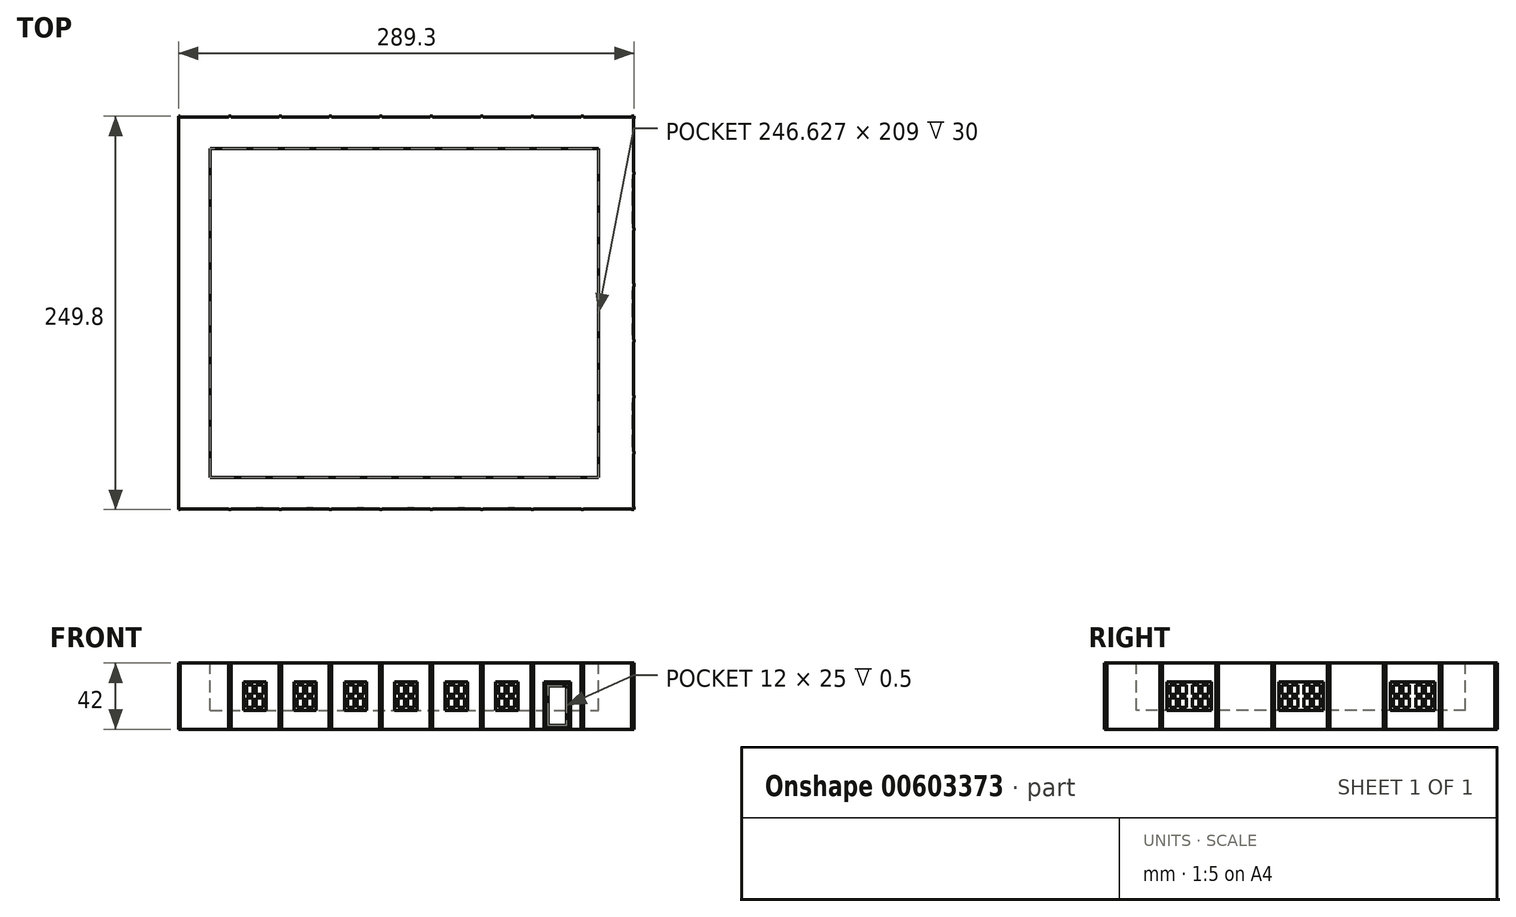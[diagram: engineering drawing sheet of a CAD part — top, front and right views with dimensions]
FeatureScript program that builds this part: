
annotation { "Feature Type Name" : "Feature", "Feature Type Description" : "" }
export const myFeature = defineFeature(function(context is Context, id is Id, definition is map)
    precondition{}
    {
        {
            var Q0;
            Q0=qCreatedBy(makeId("Top.planeOp"),FACE);
            var sketch = newSketch(context, id + "F0", { "sketchPlane" : qUnion([Q0])});
            skLineSegment(sketch, "E0", {"start": v(0, -140.86) * mm, "end": v(288.9, -140.86) * mm});
            skLineSegment(sketch, "E1", {"start": v(288.9, -140.86) * mm, "end": v(288.9, 108.14) * mm});
            skLineSegment(sketch, "E2", {"start": v(288.9, 108.14) * mm, "end": v(0, 108.14) * mm});
            skLineSegment(sketch, "E3", {"start": v(0, 108.14) * mm, "end": v(0, -140.86) * mm});
            skSolve(sketch);
        }
        {
            var Q0;
            Q0=makeQuery(id+"F0.imprint","IMPRINT",FACE,{"disambiguationData":[TD([[makeQuery(id+"F0.imprint","IMPRINT",EDGE,{"derivedFrom":sQuery(id+"F0.wireOp",EDGE,"E0")}),1.0]])]});
            extrude(context, id + "F1", {"entities" : qUnion([Q0]), "depth" : 42 * mm, "offsetDistance" : 25 * mm});
        }
        {
            var Q0;
            Q0=makeQuery(id+"F9.boolean.opBoolean","MERGE",FACE,{"derivedFrom":[makeQuery(id+"F8.boolean.opBoolean","MERGE",FACE,{"derivedFrom":[makeQuery(id+"FKC5EGcOAujftDL_1.boolean.opBoolean","MERGE",FACE,{"derivedFrom":[makeQuery(id+"F7.boolean.opBoolean","MERGE",FACE,{"derivedFrom":[makeQuery(id+"F1.opExtrude","CAP_FACE",FACE,{"disambiguationData":[OSD([sQuery(id+"F0.wireOp",EDGE,"8xd5dAzC-Wqp6-h7tH-H7tE-NGzX7Ft5cmzh"),sQuery(id+"F0.wireOp",EDGE,"hRFSEfgS-VMWt-3fDN-leBi-aHyg2lvO88b9"),sQuery(id+"F0.wireOp",EDGE,"15I0IDVO-pKoD-TTqa-lHFC-phRzDuBpSonG"),sQuery(id+"F0.wireOp",EDGE,"E9n6moV1-YT5Z-gS44-o2V7-hoNZe9HUdsiT"),sQuery(id+"F0.wireOp",EDGE,"E0"),sQuery(id+"F0.wireOp",EDGE,"E1"),sQuery(id+"F0.wireOp",EDGE,"E2"),sQuery(id+"F0.wireOp",EDGE,"iMeLHw3H-zCRP-NOLP-AAKb-Z6zfaNGieTnc"),sQuery(id+"F0.wireOp",EDGE,"wJRKMPhx-6D9Z-oqOQ-iHWZ-ZcCnmwzGZOsi"),sQuery(id+"F0.wireOp",EDGE,"79P3R2Ka-pqmj-Raxs-LlIB-3MVDgUL96paX"),sQuery(id+"F0.wireOp",EDGE,"MXDQER9f-F6fQ-SgwC-GJyv-tUGoU5TcDof0"),sQuery(id+"F0.wireOp",EDGE,"0gfRuTpH-V7bu-1aNA-bRZv-01e0o318Y1iy")])],"isStart":false}),makeQuery(id+"F7.opExtrude","SWEPT_FACE",FACE,{"disambiguationData":[OSD([sQuery(id+"Fwe09lFx9iPPisn_1.wireOp",EDGE,"jPmejYMU-EDAy-gsfS-diWM-EAnkNl0u1gXf.bottom")])]}),makeQuery(id+"F7.opExtrude","SWEPT_FACE",FACE,{"disambiguationData":[OSD([sQuery(id+"Fwe09lFx9iPPisn_1.wireOp",EDGE,"pNjlWuFm-qRlG-o4oQ-KnFu-g5xlic3dD8Ps.bottom")])]}),makeQuery(id+"F7.opExtrude","SWEPT_FACE",FACE,{"disambiguationData":[OSD([sQuery(id+"Fwe09lFx9iPPisn_1.wireOp",EDGE,"D4QHL1s9-ERpE-ATo8-meSf-Ey0yKuIFIN3O.bottom")])]}),makeQuery(id+"F7.opExtrude","SWEPT_FACE",FACE,{"disambiguationData":[OSD([sQuery(id+"Fwe09lFx9iPPisn_1.wireOp",EDGE,"y8aiQCet-G734-PklX-p9YC-myIl29S9cR5S.bottom")])]}),makeQuery(id+"F7.opExtrude","SWEPT_FACE",FACE,{"disambiguationData":[OSD([sQuery(id+"Fwe09lFx9iPPisn_1.wireOp",EDGE,"fWCZEpKj-Ez9w-WuAU-g64b-AzElcitYffAw.bottom")])]}),makeQuery(id+"F7.opExtrude","SWEPT_FACE",FACE,{"disambiguationData":[OSD([sQuery(id+"Fwe09lFx9iPPisn_1.wireOp",EDGE,"XPmMN5SE-qsZp-6xWQ-uABL-O8b3GOHQPUj3.bottom")])]}),makeQuery(id+"F7.opExtrude","SWEPT_FACE",FACE,{"disambiguationData":[OSD([sQuery(id+"Fwe09lFx9iPPisn_1.wireOp",EDGE,"Mwqcbqkp-XwH4-AiG4-FQyO-eUEv7yaxP8Wv.bottom")])]}),makeQuery(id+"F7.opExtrude","SWEPT_FACE",FACE,{"disambiguationData":[OSD([sQuery(id+"Fwe09lFx9iPPisn_1.wireOp",EDGE,"s4vkGQoF-RoVX-TYap-B4jW-lnfcoV5LbT0T.bottom")])]}),makeQuery(id+"F7.opExtrude","SWEPT_FACE",FACE,{"disambiguationData":[OSD([sQuery(id+"FwTraKnzCcuWGGP_1.wireOp",EDGE,"zttrrdUG-PdM2-wTa0-XrJa-XGaYHgbykQL0.bottom")])]}),makeQuery(id+"F7.opExtrude","SWEPT_FACE",FACE,{"disambiguationData":[OSD([sQuery(id+"FwTraKnzCcuWGGP_1.wireOp",EDGE,"9LqoM2Bj-slC5-XcZG-M1J7-WFe0YQ26WDxB.bottom")])]}),makeQuery(id+"F7.opExtrude","SWEPT_FACE",FACE,{"disambiguationData":[OSD([sQuery(id+"FwTraKnzCcuWGGP_1.wireOp",EDGE,"jVhpuxj7-Lk56-GYPV-lGb6-M2iTCW7YoZO6.bottom")])]}),makeQuery(id+"F7.opExtrude","SWEPT_FACE",FACE,{"disambiguationData":[OSD([sQuery(id+"FwTraKnzCcuWGGP_1.wireOp",EDGE,"NLwmzc69-bnuM-5JFP-S5te-JKkMOMeOY5fd.bottom")])]}),makeQuery(id+"F7.opExtrude","SWEPT_FACE",FACE,{"disambiguationData":[OSD([sQuery(id+"F4.wireOp",EDGE,"E9.bottom")])]}),makeQuery(id+"F7.opExtrude","SWEPT_FACE",FACE,{"disambiguationData":[OSD([sQuery(id+"F4.wireOp",EDGE,"E19.bottom")])]}),makeQuery(id+"F7.opExtrude","SWEPT_FACE",FACE,{"disambiguationData":[OSD([sQuery(id+"F4.wireOp",EDGE,"E20.1.0.1")])]}),makeQuery(id+"F7.opExtrude","SWEPT_FACE",FACE,{"disambiguationData":[OSD([sQuery(id+"F4.wireOp",EDGE,"E20.2.0.1")])]}),makeQuery(id+"F7.opExtrude","SWEPT_FACE",FACE,{"disambiguationData":[OSD([sQuery(id+"F4.wireOp",EDGE,"E20.3.0.1")])]}),makeQuery(id+"F7.opExtrude","SWEPT_FACE",FACE,{"disambiguationData":[OSD([sQuery(id+"F4.wireOp",EDGE,"E20.4.0.1")])]}),makeQuery(id+"F7.opExtrude","SWEPT_FACE",FACE,{"disambiguationData":[OSD([sQuery(id+"F4.wireOp",EDGE,"E20.5.0.1")])]}),makeQuery(id+"F7.opExtrude","SWEPT_FACE",FACE,{"disambiguationData":[OSD([sQuery(id+"F4.wireOp",EDGE,"E20.6.0.1")])]}),makeQuery(id+"F7.opExtrude","SWEPT_FACE",FACE,{"disambiguationData":[OSD([sQuery(id+"F4.wireOp",EDGE,"E20.7.0.1")])]}),makeQuery(id+"F7.opExtrude","SWEPT_FACE",FACE,{"disambiguationData":[OSD([sQuery(id+"F4.wireOp",EDGE,"E21.bottom")])]})]}),makeQuery(id+"FKC5EGcOAujftDL_1.opExtrude","SWEPT_FACE",FACE,{"disambiguationData":[OSD([sQuery(id+"FybVdcTg2JU70p2_1.wireOp",EDGE,"nbVrTb0j-numX-gGhW-QoSi-od30YmP2JliM.bottom")])]}),makeQuery(id+"FKC5EGcOAujftDL_1.opExtrude","SWEPT_FACE",FACE,{"disambiguationData":[OSD([sQuery(id+"FybVdcTg2JU70p2_1.wireOp",EDGE,"2qpFv3lt-VvzI-vTYO-8CgW-slAz3bjK866o.bottom")])]}),makeQuery(id+"FKC5EGcOAujftDL_1.opExtrude","SWEPT_FACE",FACE,{"disambiguationData":[OSD([sQuery(id+"Fs5d4S2FToVw5jp_1.wireOp",EDGE,"1ed185ad-1191-4033-8989-93e8961c54d0.bottom")])]}),makeQuery(id+"FKC5EGcOAujftDL_1.opExtrude","SWEPT_FACE",FACE,{"disambiguationData":[OSD([sQuery(id+"Fs5d4S2FToVw5jp_1.wireOp",EDGE,"a2324ec6-4809-4d58-a914-fea1c3dee816.1.0.1")])]}),makeQuery(id+"FKC5EGcOAujftDL_1.opExtrude","SWEPT_FACE",FACE,{"disambiguationData":[OSD([sQuery(id+"Fs5d4S2FToVw5jp_1.wireOp",EDGE,"a2324ec6-4809-4d58-a914-fea1c3dee816.2.0.1")])]}),makeQuery(id+"FKC5EGcOAujftDL_1.opExtrude","SWEPT_FACE",FACE,{"disambiguationData":[OSD([sQuery(id+"Fs5d4S2FToVw5jp_1.wireOp",EDGE,"a2324ec6-4809-4d58-a914-fea1c3dee816.3.0.1")])]}),makeQuery(id+"FKC5EGcOAujftDL_1.opExtrude","SWEPT_FACE",FACE,{"disambiguationData":[OSD([sQuery(id+"Fs5d4S2FToVw5jp_1.wireOp",EDGE,"a2324ec6-4809-4d58-a914-fea1c3dee816.4.0.1")])]}),makeQuery(id+"FKC5EGcOAujftDL_1.opExtrude","SWEPT_FACE",FACE,{"disambiguationData":[OSD([sQuery(id+"Fs5d4S2FToVw5jp_1.wireOp",EDGE,"a2324ec6-4809-4d58-a914-fea1c3dee816.5.0.1")])]}),makeQuery(id+"FKC5EGcOAujftDL_1.opExtrude","SWEPT_FACE",FACE,{"disambiguationData":[OSD([sQuery(id+"Fs5d4S2FToVw5jp_1.wireOp",EDGE,"a2324ec6-4809-4d58-a914-fea1c3dee816.6.0.1")])]}),makeQuery(id+"FKC5EGcOAujftDL_1.opExtrude","SWEPT_FACE",FACE,{"disambiguationData":[OSD([sQuery(id+"Fs5d4S2FToVw5jp_1.wireOp",EDGE,"a2324ec6-4809-4d58-a914-fea1c3dee816.7.0.1")])]}),makeQuery(id+"FKC5EGcOAujftDL_1.opExtrude","SWEPT_FACE",FACE,{"disambiguationData":[OSD([sQuery(id+"Fs5d4S2FToVw5jp_1.wireOp",EDGE,"a2324ec6-4809-4d58-a914-fea1c3dee816.8.0.1")])]}),makeQuery(id+"FKC5EGcOAujftDL_1.opExtrude","SWEPT_FACE",FACE,{"disambiguationData":[OSD([sQuery(id+"F8hd46uJ4Y0Jw0P_1.wireOp",EDGE,"g7T0L2iU-a4JC-l2rt-GfOd-ExQ9rZIDhC1y.bottom")])]}),makeQuery(id+"FKC5EGcOAujftDL_1.opExtrude","SWEPT_FACE",FACE,{"disambiguationData":[OSD([sQuery(id+"F8hd46uJ4Y0Jw0P_1.wireOp",EDGE,"nh76fuHv-sgCU-QS5b-iERR-bUxPqOiyCYYa.bottom")])]})]}),makeQuery(id+"F8.opExtrude","SWEPT_FACE",FACE,{"disambiguationData":[OSD([sQuery(id+"FUFMqIj3LLCPGwD_1.wireOp",EDGE,"2EgtnyFp-e49B-E1dY-mxFF-hXvUU2go0rJE.bottom")])]}),makeQuery(id+"F8.opExtrude","SWEPT_FACE",FACE,{"disambiguationData":[OSD([sQuery(id+"FUFMqIj3LLCPGwD_1.wireOp",EDGE,"OIG6hK1G-r6nk-9swA-24L6-EF3txMGZj8fQ.bottom")])]}),makeQuery(id+"F8.opExtrude","SWEPT_FACE",FACE,{"disambiguationData":[OSD([sQuery(id+"F5.wireOp",EDGE,"E23.bottom")])]}),makeQuery(id+"F8.opExtrude","SWEPT_FACE",FACE,{"disambiguationData":[OSD([sQuery(id+"F5.wireOp",EDGE,"E24.1.0.1")])]}),makeQuery(id+"F8.opExtrude","SWEPT_FACE",FACE,{"disambiguationData":[OSD([sQuery(id+"F5.wireOp",EDGE,"E24.2.0.1")])]}),makeQuery(id+"F8.opExtrude","SWEPT_FACE",FACE,{"disambiguationData":[OSD([sQuery(id+"F5.wireOp",EDGE,"E24.3.0.1")])]}),makeQuery(id+"F8.opExtrude","SWEPT_FACE",FACE,{"disambiguationData":[OSD([sQuery(id+"F5.wireOp",EDGE,"E24.4.0.1")])]}),makeQuery(id+"F8.opExtrude","SWEPT_FACE",FACE,{"disambiguationData":[OSD([sQuery(id+"F5.wireOp",EDGE,"E24.5.0.1")])]}),makeQuery(id+"F8.opExtrude","SWEPT_FACE",FACE,{"disambiguationData":[OSD([sQuery(id+"F5.wireOp",EDGE,"E24.6.0.1")])]}),makeQuery(id+"F8.opExtrude","SWEPT_FACE",FACE,{"disambiguationData":[OSD([sQuery(id+"F5.wireOp",EDGE,"E24.7.0.1")])]}),makeQuery(id+"F8.opExtrude","SWEPT_FACE",FACE,{"disambiguationData":[OSD([sQuery(id+"F5.wireOp",EDGE,"E24.8.0.1")])]}),makeQuery(id+"F8.opExtrude","SWEPT_FACE",FACE,{"disambiguationData":[OSD([sQuery(id+"FvbplS6eJdYwKql_1.wireOp",EDGE,"L7ZIqOHY-zK9K-wVxE-dcu3-WmX9OKhb4NxR.bottom")])]}),makeQuery(id+"F8.opExtrude","SWEPT_FACE",FACE,{"disambiguationData":[OSD([sQuery(id+"FvbplS6eJdYwKql_1.wireOp",EDGE,"Ibu1INUo-vV1Q-91VV-dQL3-sCeebD56avpD.bottom")])]})]}),makeQuery(id+"F9.opExtrude","SWEPT_FACE",FACE,{"disambiguationData":[OSD([sQuery(id+"FpW6PjU5s2u6CDz_1.wireOp",EDGE,"4fb259ca-4ae3-4482-bac9-007c0114e1a6.top")])]}),makeQuery(id+"F9.opExtrude","SWEPT_FACE",FACE,{"disambiguationData":[OSD([sQuery(id+"FpW6PjU5s2u6CDz_1.wireOp",EDGE,"5f990a85-d637-44a3-a5d5-26c224293cf6.top")])]}),makeQuery(id+"F9.opExtrude","SWEPT_FACE",FACE,{"disambiguationData":[OSD([sQuery(id+"FpW6PjU5s2u6CDz_1.wireOp",EDGE,"ca980b16-4e3a-4fdb-a5e0-f5aed0c9dccd.top")])]}),makeQuery(id+"F9.opExtrude","SWEPT_FACE",FACE,{"disambiguationData":[OSD([sQuery(id+"FpW6PjU5s2u6CDz_1.wireOp",EDGE,"cb7a1f37-ba83-463c-8abf-361e92db84c3.top")])]}),makeQuery(id+"F9.opExtrude","SWEPT_FACE",FACE,{"disambiguationData":[OSD([sQuery(id+"FpW6PjU5s2u6CDz_1.wireOp",EDGE,"d3e7f7ff-e28f-4b10-9285-89cea926f21b.top")])]}),makeQuery(id+"F9.opExtrude","SWEPT_FACE",FACE,{"disambiguationData":[OSD([sQuery(id+"FpW6PjU5s2u6CDz_1.wireOp",EDGE,"587c1e32-b4bc-4cf2-b06a-fee5fc7117d5.top")])]}),makeQuery(id+"F9.opExtrude","SWEPT_FACE",FACE,{"disambiguationData":[OSD([sQuery(id+"FpW6PjU5s2u6CDz_1.wireOp",EDGE,"a193059a-d262-4f85-8936-d8900e07d153.top")])]}),makeQuery(id+"F9.opExtrude","SWEPT_FACE",FACE,{"disambiguationData":[OSD([sQuery(id+"FpW6PjU5s2u6CDz_1.wireOp",EDGE,"f8c3b316-bbf9-46b9-b3c3-2190457b5442.top")])]}),makeQuery(id+"F9.opExtrude","SWEPT_FACE",FACE,{"disambiguationData":[OSD([sQuery(id+"Fq0A25gpBkwn3ZB_1.wireOp",EDGE,"jUTgJ92k-K5qV-ZPjf-Kwzq-RipGmp90f0id.bottom")])]}),makeQuery(id+"F9.opExtrude","SWEPT_FACE",FACE,{"disambiguationData":[OSD([sQuery(id+"Fq0A25gpBkwn3ZB_1.wireOp",EDGE,"oKRN9rtF-Zt0z-p0Hg-1U2G-0hxA56rWEqhu.bottom")])]}),makeQuery(id+"F9.opExtrude","SWEPT_FACE",FACE,{"disambiguationData":[OSD([sQuery(id+"Fq0A25gpBkwn3ZB_1.wireOp",EDGE,"g4g4EV5O-flQ6-4CuP-klBL-Wwnwc2hJ4SLr.bottom")])]}),makeQuery(id+"F9.opExtrude","SWEPT_FACE",FACE,{"disambiguationData":[OSD([sQuery(id+"Fq0A25gpBkwn3ZB_1.wireOp",EDGE,"VZhGwXNJ-cWxi-LqA3-GImR-68fYqPWMc5HT.bottom")])]}),makeQuery(id+"F9.opExtrude","SWEPT_FACE",FACE,{"disambiguationData":[OSD([sQuery(id+"F6.wireOp",EDGE,"E27.top")])]}),makeQuery(id+"F9.opExtrude","SWEPT_FACE",FACE,{"disambiguationData":[OSD([sQuery(id+"F6.wireOp",EDGE,"E37.top")])]}),makeQuery(id+"F9.opExtrude","SWEPT_FACE",FACE,{"disambiguationData":[OSD([sQuery(id+"F6.wireOp",EDGE,"E38.1.0.3")])]}),makeQuery(id+"F9.opExtrude","SWEPT_FACE",FACE,{"disambiguationData":[OSD([sQuery(id+"F6.wireOp",EDGE,"E38.2.0.3")])]}),makeQuery(id+"F9.opExtrude","SWEPT_FACE",FACE,{"disambiguationData":[OSD([sQuery(id+"F6.wireOp",EDGE,"E38.3.0.3")])]}),makeQuery(id+"F9.opExtrude","SWEPT_FACE",FACE,{"disambiguationData":[OSD([sQuery(id+"F6.wireOp",EDGE,"E38.4.0.3")])]}),makeQuery(id+"F9.opExtrude","SWEPT_FACE",FACE,{"disambiguationData":[OSD([sQuery(id+"F6.wireOp",EDGE,"E38.5.0.3")])]}),makeQuery(id+"F9.opExtrude","SWEPT_FACE",FACE,{"disambiguationData":[OSD([sQuery(id+"F6.wireOp",EDGE,"E38.6.0.3")])]}),makeQuery(id+"F9.opExtrude","SWEPT_FACE",FACE,{"disambiguationData":[OSD([sQuery(id+"F6.wireOp",EDGE,"E38.7.0.3")])]}),makeQuery(id+"F9.opExtrude","SWEPT_FACE",FACE,{"disambiguationData":[OSD([sQuery(id+"F6.wireOp",EDGE,"E39.top")])]})]});
            var sketch = newSketch(context, id + "F2", { "sketchPlane" : qUnion([Q0])});
            skLineSegment(sketch, "E4.8", {"start": v(20, -120.86) * mm, "end": v(266.63, -120.86) * mm});
            skLineSegment(sketch, "E4.9", {"start": v(266.63, -120.86) * mm, "end": v(266.63, 88.14) * mm});
            skLineSegment(sketch, "E4.10", {"start": v(266.63, 88.14) * mm, "end": v(20, 88.14) * mm});
            skPoint(sketch, "E5", {"position": v(20, -120.86) * mm});
            skPoint(sketch, "E6", {"position": v(20, 88.14) * mm});
            skLineSegment(sketch, "E7", {"start": v(20, 88.14) * mm, "end": v(20, -120.86) * mm});
            skSolve(sketch);
        }
        {
            var Q0;
            Q0=makeQuery(id+"F2.imprint","IMPRINT",FACE,{"disambiguationData":[TD([[makeQuery(id+"F2.imprint","IMPRINT",EDGE,{"derivedFrom":sQuery(id+"F2.wireOp",EDGE,"E4.8")}),1.0]])]});
            extrude(context, id + "F3", {"entities" : qUnion([Q0]), "operationType" : NewBodyOperationType.REMOVE, "oppositeDirection" : true, "depth" : 30 * mm, "offsetDistance" : 25 * mm});
        }
        {
            var Q0;
            Q0=makeQuery(id+"F1.opExtrude","SWEPT_FACE",FACE,{"disambiguationData":[OSD([sQuery(id+"F0.wireOp",EDGE,"E0")])]});
            var sketch = newSketch(context, id + "F4", { "sketchPlane" : qUnion([Q0])});
            skPoint(sketch, "E8", {"position": v(287.7, 42) * mm});
            skLineSegment(sketch, "E9.bottom", {"start": v(287.7, 42) * mm, "end": v(289.3, 42) * mm});
            skLineSegment(sketch, "E9.top", {"start": v(287.7, 0) * mm, "end": v(289.3, 0) * mm});
            skLineSegment(sketch, "E9.left", {"start": v(287.7, 42) * mm, "end": v(287.7, 0) * mm});
            skLineSegment(sketch, "E9.right", {"start": v(289.3, 42) * mm, "end": v(289.3, 0) * mm});
            skPoint(sketch, "E10", {"position": v(288.5, 42) * mm});
            skPoint(sketch, "E11", {"position": v(256.5, 42) * mm});
            skPoint(sketch, "E12", {"position": v(224.5, 42) * mm});
            skPoint(sketch, "E13", {"position": v(192.5, 42) * mm});
            skPoint(sketch, "E14", {"position": v(160.5, 42) * mm});
            skPoint(sketch, "E15", {"position": v(128.5, 42) * mm});
            skPoint(sketch, "E16", {"position": v(96.5, 42) * mm});
            skPoint(sketch, "E17", {"position": v(64.5, 42) * mm});
            skPoint(sketch, "E18", {"position": v(32.5, 42) * mm});
            skLineSegment(sketch, "E19.bottom", {"start": v(255.7, 42) * mm, "end": v(257.3, 42) * mm});
            skLineSegment(sketch, "E19.top", {"start": v(255.7, 0) * mm, "end": v(257.3, 0) * mm});
            skLineSegment(sketch, "E19.left", {"start": v(255.7, 42) * mm, "end": v(255.7, 0) * mm});
            skLineSegment(sketch, "E19.right", {"start": v(257.3, 42) * mm, "end": v(257.3, 0) * mm});
            skLineSegment(sketch, "E20.1.0.0", {"start": v(223.7, 42) * mm, "end": v(223.7, 0) * mm});
            skLineSegment(sketch, "E20.1.0.1", {"start": v(223.7, 42) * mm, "end": v(225.3, 42) * mm});
            skLineSegment(sketch, "E20.1.0.2", {"start": v(225.3, 42) * mm, "end": v(225.3, 0) * mm});
            skLineSegment(sketch, "E20.1.0.3", {"start": v(223.7, 0) * mm, "end": v(225.3, 0) * mm});
            skLineSegment(sketch, "E20.2.0.0", {"start": v(191.7, 42) * mm, "end": v(191.7, 0) * mm});
            skLineSegment(sketch, "E20.2.0.1", {"start": v(191.7, 42) * mm, "end": v(193.3, 42) * mm});
            skLineSegment(sketch, "E20.2.0.2", {"start": v(193.3, 42) * mm, "end": v(193.3, 0) * mm});
            skLineSegment(sketch, "E20.2.0.3", {"start": v(191.7, 0) * mm, "end": v(193.3, 0) * mm});
            skLineSegment(sketch, "E20.3.0.0", {"start": v(159.7, 42) * mm, "end": v(159.7, 0) * mm});
            skLineSegment(sketch, "E20.3.0.1", {"start": v(159.7, 42) * mm, "end": v(161.3, 42) * mm});
            skLineSegment(sketch, "E20.3.0.2", {"start": v(161.3, 42) * mm, "end": v(161.3, 0) * mm});
            skLineSegment(sketch, "E20.3.0.3", {"start": v(159.7, 0) * mm, "end": v(161.3, 0) * mm});
            skLineSegment(sketch, "E20.4.0.0", {"start": v(127.7, 42) * mm, "end": v(127.7, 0) * mm});
            skLineSegment(sketch, "E20.4.0.1", {"start": v(127.7, 42) * mm, "end": v(129.3, 42) * mm});
            skLineSegment(sketch, "E20.4.0.2", {"start": v(129.3, 42) * mm, "end": v(129.3, 0) * mm});
            skLineSegment(sketch, "E20.4.0.3", {"start": v(127.7, 0) * mm, "end": v(129.3, 0) * mm});
            skLineSegment(sketch, "E20.5.0.0", {"start": v(95.7, 42) * mm, "end": v(95.7, 0) * mm});
            skLineSegment(sketch, "E20.5.0.1", {"start": v(95.7, 42) * mm, "end": v(97.3, 42) * mm});
            skLineSegment(sketch, "E20.5.0.2", {"start": v(97.3, 42) * mm, "end": v(97.3, 0) * mm});
            skLineSegment(sketch, "E20.5.0.3", {"start": v(95.7, 0) * mm, "end": v(97.3, 0) * mm});
            skLineSegment(sketch, "E20.6.0.0", {"start": v(63.7, 42) * mm, "end": v(63.7, 0) * mm});
            skLineSegment(sketch, "E20.6.0.1", {"start": v(63.7, 42) * mm, "end": v(65.3, 42) * mm});
            skLineSegment(sketch, "E20.6.0.2", {"start": v(65.3, 42) * mm, "end": v(65.3, 0) * mm});
            skLineSegment(sketch, "E20.6.0.3", {"start": v(63.7, 0) * mm, "end": v(65.3, 0) * mm});
            skLineSegment(sketch, "E20.7.0.0", {"start": v(31.7, 42) * mm, "end": v(31.7, 0) * mm});
            skLineSegment(sketch, "E20.7.0.1", {"start": v(31.7, 42) * mm, "end": v(33.3, 42) * mm});
            skLineSegment(sketch, "E20.7.0.2", {"start": v(33.3, 42) * mm, "end": v(33.3, 0) * mm});
            skLineSegment(sketch, "E20.7.0.3", {"start": v(31.7, 0) * mm, "end": v(33.3, 0) * mm});
            skLineSegment(sketch, "E20.direction1", {"start": v(255.7, 0) * mm, "end": v(223.7, 0) * mm, "construction": true});
            skLineSegment(sketch, "E21.bottom", {"start": v(0, 42) * mm, "end": v(0.8, 42) * mm});
            skLineSegment(sketch, "E21.top", {"start": v(0, 0) * mm, "end": v(0.8, 0) * mm});
            skLineSegment(sketch, "E21.left", {"start": v(0, 42) * mm, "end": v(0, 0) * mm});
            skLineSegment(sketch, "E21.right", {"start": v(0.8, 42) * mm, "end": v(0.8, 0) * mm});
            skSolve(sketch);
        }
        {
            var Q0;
            Q0=makeQuery(id+"F1.opExtrude","SWEPT_FACE",FACE,{"disambiguationData":[OSD([sQuery(id+"F0.wireOp",EDGE,"E1")])]});
            var sketch = newSketch(context, id + "F5", { "sketchPlane" : qUnion([Q0])});
            skPoint(sketch, "E22", {"position": v(-139.66, 42) * mm});
            skLineSegment(sketch, "E23.bottom", {"start": v(-139.66, 42) * mm, "end": v(-141.26, 42) * mm});
            skLineSegment(sketch, "E23.top", {"start": v(-139.66, 0) * mm, "end": v(-141.26, 0) * mm});
            skLineSegment(sketch, "E23.left", {"start": v(-139.66, 42) * mm, "end": v(-139.66, 0) * mm});
            skLineSegment(sketch, "E23.right", {"start": v(-141.26, 42) * mm, "end": v(-141.26, 0) * mm});
            skLineSegment(sketch, "E24.1.0.0", {"start": v(-104.2, 42) * mm, "end": v(-104.2, 0) * mm});
            skLineSegment(sketch, "E24.1.0.1", {"start": v(-104.2, 42) * mm, "end": v(-105.8, 42) * mm});
            skLineSegment(sketch, "E24.1.0.2", {"start": v(-105.8, 42) * mm, "end": v(-105.8, 0) * mm});
            skLineSegment(sketch, "E24.1.0.3", {"start": v(-104.2, 0) * mm, "end": v(-105.8, 0) * mm});
            skLineSegment(sketch, "E24.2.0.0", {"start": v(-68.74, 42) * mm, "end": v(-68.74, 0) * mm});
            skLineSegment(sketch, "E24.2.0.1", {"start": v(-68.74, 42) * mm, "end": v(-70.34, 42) * mm});
            skLineSegment(sketch, "E24.2.0.2", {"start": v(-70.34, 42) * mm, "end": v(-70.34, 0) * mm});
            skLineSegment(sketch, "E24.2.0.3", {"start": v(-68.74, 0) * mm, "end": v(-70.34, 0) * mm});
            skLineSegment(sketch, "E24.3.0.0", {"start": v(-33.29, 42) * mm, "end": v(-33.29, 0) * mm});
            skLineSegment(sketch, "E24.3.0.1", {"start": v(-33.29, 42) * mm, "end": v(-34.89, 42) * mm});
            skLineSegment(sketch, "E24.3.0.2", {"start": v(-34.89, 42) * mm, "end": v(-34.89, 0) * mm});
            skLineSegment(sketch, "E24.3.0.3", {"start": v(-33.29, 0) * mm, "end": v(-34.89, 0) * mm});
            skLineSegment(sketch, "E24.4.0.0", {"start": v(2.17, 42) * mm, "end": v(2.17, 0) * mm});
            skLineSegment(sketch, "E24.4.0.1", {"start": v(2.17, 42) * mm, "end": v(0.57, 42) * mm});
            skLineSegment(sketch, "E24.4.0.2", {"start": v(0.57, 42) * mm, "end": v(0.57, 0) * mm});
            skLineSegment(sketch, "E24.4.0.3", {"start": v(2.17, 0) * mm, "end": v(0.57, 0) * mm});
            skLineSegment(sketch, "E24.5.0.0", {"start": v(37.63, 42) * mm, "end": v(37.63, 0) * mm});
            skLineSegment(sketch, "E24.5.0.1", {"start": v(37.63, 42) * mm, "end": v(36.03, 42) * mm});
            skLineSegment(sketch, "E24.5.0.2", {"start": v(36.03, 42) * mm, "end": v(36.03, 0) * mm});
            skLineSegment(sketch, "E24.5.0.3", {"start": v(37.63, 0) * mm, "end": v(36.03, 0) * mm});
            skLineSegment(sketch, "E24.6.0.0", {"start": v(73.09, 42) * mm, "end": v(73.09, 0) * mm});
            skLineSegment(sketch, "E24.6.0.1", {"start": v(73.09, 42) * mm, "end": v(71.49, 42) * mm});
            skLineSegment(sketch, "E24.6.0.2", {"start": v(71.49, 42) * mm, "end": v(71.49, 0) * mm});
            skLineSegment(sketch, "E24.6.0.3", {"start": v(73.09, 0) * mm, "end": v(71.49, 0) * mm});
            skLineSegment(sketch, "E24.direction1", {"start": v(-139.66, 0) * mm, "end": v(-104.2, 0) * mm, "construction": true});
            skLineSegment(sketch, "E25.0.7.0", {"start": v(108.54, 42) * mm, "end": v(108.54, 0) * mm});
            skLineSegment(sketch, "E25.3.7.0", {"start": v(108.54, 42) * mm, "end": v(106.94, 42) * mm});
            skLineSegment(sketch, "E25.6.7.0", {"start": v(106.94, 42) * mm, "end": v(106.94, 0) * mm});
            skLineSegment(sketch, "E25.9.7.0", {"start": v(108.54, 0) * mm, "end": v(106.94, 0) * mm});
            skSolve(sketch);
        }
        {
            var Q0;
            Q0=makeQuery(id+"F1.opExtrude","SWEPT_FACE",FACE,{"disambiguationData":[OSD([sQuery(id+"F0.wireOp",EDGE,"E2")])]});
            var sketch = newSketch(context, id + "F6", { "sketchPlane" : qUnion([Q0])});
            skPoint(sketch, "E26", {"position": v(-287.7, 0) * mm});
            skLineSegment(sketch, "E27.bottom", {"start": v(-287.7, 0) * mm, "end": v(-289.3, 0) * mm});
            skLineSegment(sketch, "E27.top", {"start": v(-287.7, 42) * mm, "end": v(-289.3, 42) * mm});
            skLineSegment(sketch, "E27.left", {"start": v(-287.7, 0) * mm, "end": v(-287.7, 42) * mm});
            skLineSegment(sketch, "E27.right", {"start": v(-289.3, 0) * mm, "end": v(-289.3, 42) * mm});
            skPoint(sketch, "E28", {"position": v(-288.5, 0) * mm});
            skPoint(sketch, "E29", {"position": v(-256.5, 0) * mm});
            skPoint(sketch, "E30", {"position": v(-224.5, 0) * mm});
            skPoint(sketch, "E31", {"position": v(-192.5, 0) * mm});
            skPoint(sketch, "E32", {"position": v(-160.5, 0) * mm});
            skPoint(sketch, "E33", {"position": v(-128.5, 0) * mm});
            skPoint(sketch, "E34", {"position": v(-96.5, 0) * mm});
            skPoint(sketch, "E35", {"position": v(-64.5, 0) * mm});
            skPoint(sketch, "E36", {"position": v(-32.5, 0) * mm});
            skLineSegment(sketch, "E37.bottom", {"start": v(-255.7, 0) * mm, "end": v(-257.3, 0) * mm});
            skLineSegment(sketch, "E37.top", {"start": v(-255.7, 42) * mm, "end": v(-257.3, 42) * mm});
            skLineSegment(sketch, "E37.left", {"start": v(-255.7, 0) * mm, "end": v(-255.7, 42) * mm});
            skLineSegment(sketch, "E37.right", {"start": v(-257.3, 0) * mm, "end": v(-257.3, 42) * mm});
            skLineSegment(sketch, "E38.1.0.0", {"start": v(-223.7, 0) * mm, "end": v(-223.7, 42) * mm});
            skLineSegment(sketch, "E38.1.0.1", {"start": v(-223.7, 0) * mm, "end": v(-225.3, 0) * mm});
            skLineSegment(sketch, "E38.1.0.2", {"start": v(-225.3, 0) * mm, "end": v(-225.3, 42) * mm});
            skLineSegment(sketch, "E38.1.0.3", {"start": v(-223.7, 42) * mm, "end": v(-225.3, 42) * mm});
            skLineSegment(sketch, "E38.2.0.0", {"start": v(-191.7, 0) * mm, "end": v(-191.7, 42) * mm});
            skLineSegment(sketch, "E38.2.0.1", {"start": v(-191.7, 0) * mm, "end": v(-193.3, 0) * mm});
            skLineSegment(sketch, "E38.2.0.2", {"start": v(-193.3, 0) * mm, "end": v(-193.3, 42) * mm});
            skLineSegment(sketch, "E38.2.0.3", {"start": v(-191.7, 42) * mm, "end": v(-193.3, 42) * mm});
            skLineSegment(sketch, "E38.3.0.0", {"start": v(-159.7, 0) * mm, "end": v(-159.7, 42) * mm});
            skLineSegment(sketch, "E38.3.0.1", {"start": v(-159.7, 0) * mm, "end": v(-161.3, 0) * mm});
            skLineSegment(sketch, "E38.3.0.2", {"start": v(-161.3, 0) * mm, "end": v(-161.3, 42) * mm});
            skLineSegment(sketch, "E38.3.0.3", {"start": v(-159.7, 42) * mm, "end": v(-161.3, 42) * mm});
            skLineSegment(sketch, "E38.4.0.0", {"start": v(-127.7, 0) * mm, "end": v(-127.7, 42) * mm});
            skLineSegment(sketch, "E38.4.0.1", {"start": v(-127.7, 0) * mm, "end": v(-129.3, 0) * mm});
            skLineSegment(sketch, "E38.4.0.2", {"start": v(-129.3, 0) * mm, "end": v(-129.3, 42) * mm});
            skLineSegment(sketch, "E38.4.0.3", {"start": v(-127.7, 42) * mm, "end": v(-129.3, 42) * mm});
            skLineSegment(sketch, "E38.5.0.0", {"start": v(-95.7, 0) * mm, "end": v(-95.7, 42) * mm});
            skLineSegment(sketch, "E38.5.0.1", {"start": v(-95.7, 0) * mm, "end": v(-97.3, 0) * mm});
            skLineSegment(sketch, "E38.5.0.2", {"start": v(-97.3, 0) * mm, "end": v(-97.3, 42) * mm});
            skLineSegment(sketch, "E38.5.0.3", {"start": v(-95.7, 42) * mm, "end": v(-97.3, 42) * mm});
            skLineSegment(sketch, "E38.6.0.0", {"start": v(-63.7, 0) * mm, "end": v(-63.7, 42) * mm});
            skLineSegment(sketch, "E38.6.0.1", {"start": v(-63.7, 0) * mm, "end": v(-65.3, 0) * mm});
            skLineSegment(sketch, "E38.6.0.2", {"start": v(-65.3, 0) * mm, "end": v(-65.3, 42) * mm});
            skLineSegment(sketch, "E38.6.0.3", {"start": v(-63.7, 42) * mm, "end": v(-65.3, 42) * mm});
            skLineSegment(sketch, "E38.7.0.0", {"start": v(-31.7, 0) * mm, "end": v(-31.7, 42) * mm});
            skLineSegment(sketch, "E38.7.0.1", {"start": v(-31.7, 0) * mm, "end": v(-33.3, 0) * mm});
            skLineSegment(sketch, "E38.7.0.2", {"start": v(-33.3, 0) * mm, "end": v(-33.3, 42) * mm});
            skLineSegment(sketch, "E38.7.0.3", {"start": v(-31.7, 42) * mm, "end": v(-33.3, 42) * mm});
            skLineSegment(sketch, "E38.direction1", {"start": v(-255.7, 42) * mm, "end": v(-223.7, 42) * mm, "construction": true});
            skLineSegment(sketch, "E39.bottom", {"start": v(0, 0) * mm, "end": v(-0.8, 0) * mm});
            skLineSegment(sketch, "E39.top", {"start": v(0, 42) * mm, "end": v(-0.8, 42) * mm});
            skLineSegment(sketch, "E39.left", {"start": v(0, 0) * mm, "end": v(0, 42) * mm});
            skLineSegment(sketch, "E39.right", {"start": v(-0.8, 0) * mm, "end": v(-0.8, 42) * mm});
            skSolve(sketch);
        }
        {
            var Q0;
            Q0=qSketchRegion(id+"Fwe09lFx9iPPisn_1",true);
            var Q1;
            Q1=qSketchRegion(id+"FwTraKnzCcuWGGP_1",true);
            var Q2;
            Q2=qSketchRegion(id+"F4",true);
            extrude(context, id + "F7", {"entities" : qUnion([Q0, Q1, Q2]), "operationType" : NewBodyOperationType.ADD, "depth" : .4 * mm, "offsetDistance" : 25 * mm});
        }
        {
            var Q0;
            Q0=qSketchRegion(id+"FUFMqIj3LLCPGwD_1",true);
            var Q1;
            Q1=qSketchRegion(id+"F5",true);
            var Q2;
            Q2=qSketchRegion(id+"FvbplS6eJdYwKql_1",true);
            extrude(context, id + "F8", {"entities" : qUnion([Q0, Q1, Q2]), "operationType" : NewBodyOperationType.ADD, "depth" : .4 * mm, "offsetDistance" : 25 * mm});
        }
        {
            var Q0;
            Q0=qSketchRegion(id+"FpW6PjU5s2u6CDz_1",true);
            var Q1;
            Q1=qSketchRegion(id+"Fq0A25gpBkwn3ZB_1",true);
            var Q2;
            Q2=qSketchRegion(id+"F6",true);
            extrude(context, id + "F9", {"entities" : qUnion([Q0, Q1, Q2]), "operationType" : NewBodyOperationType.ADD, "depth" : .4 * mm, "offsetDistance" : 25 * mm});
        }
        {
            var Q0;
            {var subQ7=sQuery(id+"F0.wireOp",EDGE,"E0");Q0=makeQuery(id+"F7.boolean.opBoolean","SPLIT",FACE,{"disambiguationData":[TD([makeQuery(id+"F7.opExtrude","SWEPT_FACE",FACE,{"disambiguationData":[OSD([sQuery(id+"F4.wireOp",EDGE,"E19.left")])]})])],"derivedFrom":makeQuery(id+"F1.opExtrude","SWEPT_FACE",FACE,{"disambiguationData":[OSD([subQ7])]})});}
            var sketch = newSketch(context, id + "F10", { "sketchPlane" : qUnion([Q0])});
            skLineSegment(sketch, "E40.bottom", {"start": v(232, 30) * mm, "end": v(249, 30) * mm});
            skLineSegment(sketch, "E40.top", {"start": v(232, 0) * mm, "end": v(249, 0) * mm});
            skLineSegment(sketch, "E40.left", {"start": v(232, 30) * mm, "end": v(232, 0) * mm});
            skLineSegment(sketch, "E40.right", {"start": v(249, 30) * mm, "end": v(249, 0) * mm});
            skLineSegment(sketch, "E41.0", {"start": v(233, 29) * mm, "end": v(233, 1) * mm});
            skLineSegment(sketch, "E41.1", {"start": v(233, 29) * mm, "end": v(248, 29) * mm});
            skLineSegment(sketch, "E41.2", {"start": v(248, 29) * mm, "end": v(248, 1) * mm});
            skLineSegment(sketch, "E41.3", {"start": v(233, 1) * mm, "end": v(248, 1) * mm});
            skLineSegment(sketch, "E42.0", {"start": v(234.5, 27.5) * mm, "end": v(234.5, 2.5) * mm});
            skLineSegment(sketch, "E42.1", {"start": v(234.5, 27.5) * mm, "end": v(246.5, 27.5) * mm});
            skLineSegment(sketch, "E42.2", {"start": v(246.5, 27.5) * mm, "end": v(246.5, 2.5) * mm});
            skLineSegment(sketch, "E42.3", {"start": v(234.5, 2.5) * mm, "end": v(246.5, 2.5) * mm});
            skPoint(sketch, "E43", {"position": v(240.5, 0) * mm});
            skSolve(sketch);
        }
        {
            var Q0;
            Q0=makeQuery(id+"F10.imprint","IMPRINT",FACE,{"disambiguationData":[TD([[makeQuery(id+"F10.imprint","IMPRINT",EDGE,{"derivedFrom":sQuery(id+"F10.wireOp",EDGE,"E40.bottom")}),-1.0]])]});
            var Q1;
            Q1=makeQuery(id+"F10.imprint","IMPRINT",FACE,{"disambiguationData":[TD([[makeQuery(id+"F10.imprint","IMPRINT",EDGE,{"derivedFrom":sQuery(id+"F10.wireOp",EDGE,"E42.0")}),1.0]])]});
            extrude(context, id + "F11", {"entities" : qUnion([Q0, Q1]), "operationType" : NewBodyOperationType.REMOVE, "oppositeDirection" : true, "depth" : .5 * mm, "offsetDistance" : 25 * mm});
        }
        {
            var Q0;
            {var subQ6=sQuery(id+"F0.wireOp",EDGE,"E1");Q0=makeQuery(id+"F8.boolean.opBoolean","SPLIT",FACE,{"disambiguationData":[TD([makeQuery(id+"F8.opExtrude","SWEPT_FACE",FACE,{"disambiguationData":[OSD([sQuery(id+"F5.wireOp",EDGE,"E24.1.0.0")])]})])],"derivedFrom":makeQuery(id+"F1.opExtrude","SWEPT_FACE",FACE,{"disambiguationData":[OSD([subQ6])]})});}
            var sketch = newSketch(context, id + "F12", { "sketchPlane" : qUnion([Q0])});
            skLineSegment(sketch, "E44.bottom", {"start": v(-101.41, 30) * mm, "end": v(-87.27, 30) * mm});
            skLineSegment(sketch, "E44.top", {"start": v(-101.41, 12) * mm, "end": v(-87.27, 12) * mm});
            skLineSegment(sketch, "E44.left", {"start": v(-101.41, 30) * mm, "end": v(-101.41, 12) * mm});
            skLineSegment(sketch, "E44.right", {"start": v(-87.27, 30) * mm, "end": v(-87.27, 12) * mm});
            skLineSegment(sketch, "E45.0", {"start": v(-99.49, 28.07) * mm, "end": v(-95.3, 28.07) * mm});
            skLineSegment(sketch, "E45.1", {"start": v(-99.49, 28.07) * mm, "end": v(-99.49, 21.96) * mm});
            skLineSegment(sketch, "E45.2", {"start": v(-99.49, 13.93) * mm, "end": v(-95.3, 13.93) * mm});
            skLineSegment(sketch, "E45.3", {"start": v(-89.2, 28.07) * mm, "end": v(-89.2, 21.96) * mm});
            skLineSegment(sketch, "E46.left", {"start": v(-95.3, 28.07) * mm, "end": v(-95.3, 21.96) * mm});
            skLineSegment(sketch, "E46.right", {"start": v(-93.38, 28.07) * mm, "end": v(-93.38, 21.96) * mm});
            skLineSegment(sketch, "E47.bottom", {"start": v(-89.2, 21.96) * mm, "end": v(-93.38, 21.96) * mm});
            skLineSegment(sketch, "E47.top", {"start": v(-89.2, 20.04) * mm, "end": v(-93.38, 20.04) * mm});
            skLineSegment(sketch, "E48.trimOffspring", {"start": v(-95.3, 21.96) * mm, "end": v(-99.49, 21.96) * mm});
            skLineSegment(sketch, "E49.trimOffspring", {"start": v(-95.3, 20.04) * mm, "end": v(-95.3, 13.93) * mm});
            skLineSegment(sketch, "E50.trimOffspring", {"start": v(-95.3, 20.04) * mm, "end": v(-99.49, 20.04) * mm});
            skLineSegment(sketch, "E51.trimOffspring", {"start": v(-93.38, 20.04) * mm, "end": v(-93.38, 13.93) * mm});
            skLineSegment(sketch, "E52.trimOffspring", {"start": v(-89.2, 20.04) * mm, "end": v(-89.2, 13.93) * mm});
            skLineSegment(sketch, "E53.trimOffspring", {"start": v(-99.49, 20.04) * mm, "end": v(-99.49, 13.93) * mm});
            skLineSegment(sketch, "E54.trimOffspring", {"start": v(-93.38, 28.07) * mm, "end": v(-89.2, 28.07) * mm});
            skLineSegment(sketch, "E55.trimOffspring", {"start": v(-93.38, 13.93) * mm, "end": v(-89.2, 13.93) * mm});
            skLineSegment(sketch, "E56.bottom", {"start": v(-87.27, 30) * mm, "end": v(-73.13, 30) * mm});
            skLineSegment(sketch, "E56.top", {"start": v(-87.27, 12) * mm, "end": v(-73.13, 12) * mm});
            skLineSegment(sketch, "E56.right", {"start": v(-73.13, 30) * mm, "end": v(-73.13, 12) * mm});
            skLineSegment(sketch, "E57.0", {"start": v(-85.34, 28.07) * mm, "end": v(-81.16, 28.07) * mm});
            skLineSegment(sketch, "E57.1", {"start": v(-85.34, 28.07) * mm, "end": v(-85.34, 21.96) * mm});
            skLineSegment(sketch, "E57.2", {"start": v(-85.34, 13.93) * mm, "end": v(-81.16, 13.93) * mm});
            skLineSegment(sketch, "E57.3", {"start": v(-75.06, 28.07) * mm, "end": v(-75.06, 21.96) * mm});
            skLineSegment(sketch, "E58.left", {"start": v(-81.16, 28.07) * mm, "end": v(-81.16, 21.96) * mm});
            skLineSegment(sketch, "E58.right", {"start": v(-79.24, 28.07) * mm, "end": v(-79.24, 21.96) * mm});
            skLineSegment(sketch, "E59.bottom", {"start": v(-75.06, 21.96) * mm, "end": v(-79.24, 21.96) * mm});
            skLineSegment(sketch, "E59.top", {"start": v(-75.06, 20.04) * mm, "end": v(-79.24, 20.04) * mm});
            skLineSegment(sketch, "E60.trimOffspring", {"start": v(-81.16, 21.96) * mm, "end": v(-85.34, 21.96) * mm});
            skLineSegment(sketch, "E61.trimOffspring", {"start": v(-81.16, 20.04) * mm, "end": v(-81.16, 13.93) * mm});
            skLineSegment(sketch, "E62.trimOffspring", {"start": v(-81.16, 20.04) * mm, "end": v(-85.34, 20.04) * mm});
            skLineSegment(sketch, "E63.trimOffspring", {"start": v(-79.24, 20.04) * mm, "end": v(-79.24, 13.93) * mm});
            skLineSegment(sketch, "E64.trimOffspring", {"start": v(-75.06, 20.04) * mm, "end": v(-75.06, 13.93) * mm});
            skLineSegment(sketch, "E65.trimOffspring", {"start": v(-85.34, 20.04) * mm, "end": v(-85.34, 13.93) * mm});
            skLineSegment(sketch, "E66.trimOffspring", {"start": v(-79.24, 28.07) * mm, "end": v(-75.06, 28.07) * mm});
            skLineSegment(sketch, "E67.trimOffspring", {"start": v(-79.24, 13.93) * mm, "end": v(-75.06, 13.93) * mm});
            skSolve(sketch);
        }
        {
            var Q0;
            {var subQ6=sQuery(id+"F0.wireOp",EDGE,"E1");Q0=makeQuery(id+"F8.boolean.opBoolean","SPLIT",FACE,{"disambiguationData":[TD([makeQuery(id+"F8.opExtrude","SWEPT_FACE",FACE,{"disambiguationData":[OSD([sQuery(id+"F5.wireOp",EDGE,"E24.3.0.0")])]})])],"derivedFrom":makeQuery(id+"F1.opExtrude","SWEPT_FACE",FACE,{"disambiguationData":[OSD([subQ6])]})});}
            var sketch = newSketch(context, id + "F13", { "sketchPlane" : qUnion([Q0])});
            skLineSegment(sketch, "E68.bottom", {"start": v(-30.5, 30) * mm, "end": v(-16.36, 30) * mm});
            skLineSegment(sketch, "E68.top", {"start": v(-30.5, 12) * mm, "end": v(-16.36, 12) * mm});
            skLineSegment(sketch, "E68.left", {"start": v(-30.5, 30) * mm, "end": v(-30.5, 12) * mm});
            skLineSegment(sketch, "E68.right", {"start": v(-16.36, 30) * mm, "end": v(-16.36, 12) * mm});
            skLineSegment(sketch, "E69.0", {"start": v(-28.57, 28.07) * mm, "end": v(-24.4, 28.07) * mm});
            skLineSegment(sketch, "E69.1", {"start": v(-28.57, 28.07) * mm, "end": v(-28.57, 21.96) * mm});
            skLineSegment(sketch, "E69.2", {"start": v(-28.57, 13.93) * mm, "end": v(-24.4, 13.93) * mm});
            skLineSegment(sketch, "E69.3", {"start": v(-18.29, 28.07) * mm, "end": v(-18.29, 21.96) * mm});
            skLineSegment(sketch, "E70.left", {"start": v(-24.4, 28.07) * mm, "end": v(-24.4, 21.96) * mm});
            skLineSegment(sketch, "E70.right", {"start": v(-22.46, 28.07) * mm, "end": v(-22.46, 21.96) * mm});
            skLineSegment(sketch, "E71.bottom", {"start": v(-18.29, 21.96) * mm, "end": v(-22.46, 21.96) * mm});
            skLineSegment(sketch, "E71.top", {"start": v(-18.29, 20.04) * mm, "end": v(-22.46, 20.04) * mm});
            skLineSegment(sketch, "E72.trimOffspring", {"start": v(-24.4, 21.96) * mm, "end": v(-28.57, 21.96) * mm});
            skLineSegment(sketch, "E73.trimOffspring", {"start": v(-24.4, 20.04) * mm, "end": v(-24.4, 13.93) * mm});
            skLineSegment(sketch, "E74.trimOffspring", {"start": v(-24.4, 20.04) * mm, "end": v(-28.57, 20.04) * mm});
            skLineSegment(sketch, "E75.trimOffspring", {"start": v(-22.46, 20.04) * mm, "end": v(-22.46, 13.93) * mm});
            skLineSegment(sketch, "E76.trimOffspring", {"start": v(-18.29, 20.04) * mm, "end": v(-18.29, 13.93) * mm});
            skLineSegment(sketch, "E77.trimOffspring", {"start": v(-28.57, 20.04) * mm, "end": v(-28.57, 13.93) * mm});
            skLineSegment(sketch, "E78.trimOffspring", {"start": v(-22.46, 28.07) * mm, "end": v(-18.29, 28.07) * mm});
            skLineSegment(sketch, "E79.trimOffspring", {"start": v(-22.46, 13.93) * mm, "end": v(-18.29, 13.93) * mm});
            skLineSegment(sketch, "E80.bottom", {"start": v(-16.36, 30) * mm, "end": v(-2.21, 30) * mm});
            skLineSegment(sketch, "E80.top", {"start": v(-16.36, 12) * mm, "end": v(-2.21, 12) * mm});
            skLineSegment(sketch, "E80.right", {"start": v(-2.21, 30) * mm, "end": v(-2.21, 12) * mm});
            skLineSegment(sketch, "E81.0", {"start": v(-14.43, 28.07) * mm, "end": v(-10.25, 28.07) * mm});
            skLineSegment(sketch, "E81.1", {"start": v(-14.43, 28.07) * mm, "end": v(-14.43, 21.96) * mm});
            skLineSegment(sketch, "E81.2", {"start": v(-14.43, 13.93) * mm, "end": v(-10.25, 13.93) * mm});
            skLineSegment(sketch, "E81.3", {"start": v(-4.14, 28.07) * mm, "end": v(-4.14, 21.96) * mm});
            skLineSegment(sketch, "E82.left", {"start": v(-10.25, 28.07) * mm, "end": v(-10.25, 21.96) * mm});
            skLineSegment(sketch, "E82.right", {"start": v(-8.32, 28.07) * mm, "end": v(-8.32, 21.96) * mm});
            skLineSegment(sketch, "E83.bottom", {"start": v(-4.14, 21.96) * mm, "end": v(-8.32, 21.96) * mm});
            skLineSegment(sketch, "E83.top", {"start": v(-4.14, 20.04) * mm, "end": v(-8.32, 20.04) * mm});
            skLineSegment(sketch, "E84.trimOffspring", {"start": v(-10.25, 21.96) * mm, "end": v(-14.43, 21.96) * mm});
            skLineSegment(sketch, "E85.trimOffspring", {"start": v(-10.25, 20.04) * mm, "end": v(-10.25, 13.93) * mm});
            skLineSegment(sketch, "E86.trimOffspring", {"start": v(-10.25, 20.04) * mm, "end": v(-14.43, 20.04) * mm});
            skLineSegment(sketch, "E87.trimOffspring", {"start": v(-8.32, 20.04) * mm, "end": v(-8.32, 13.93) * mm});
            skLineSegment(sketch, "E88.trimOffspring", {"start": v(-4.14, 20.04) * mm, "end": v(-4.14, 13.93) * mm});
            skLineSegment(sketch, "E89.trimOffspring", {"start": v(-14.43, 20.04) * mm, "end": v(-14.43, 13.93) * mm});
            skLineSegment(sketch, "E90.trimOffspring", {"start": v(-8.32, 28.07) * mm, "end": v(-4.14, 28.07) * mm});
            skLineSegment(sketch, "E91.trimOffspring", {"start": v(-8.32, 13.93) * mm, "end": v(-4.14, 13.93) * mm});
            skSolve(sketch);
        }
        {
            var Q0;
            {var subQ6=sQuery(id+"F0.wireOp",EDGE,"E1");Q0=makeQuery(id+"F8.boolean.opBoolean","SPLIT",FACE,{"disambiguationData":[TD([makeQuery(id+"F8.opExtrude","SWEPT_FACE",FACE,{"disambiguationData":[OSD([sQuery(id+"F5.wireOp",EDGE,"E24.5.0.0")])]})])],"derivedFrom":makeQuery(id+"F1.opExtrude","SWEPT_FACE",FACE,{"disambiguationData":[OSD([subQ6])]})});}
            var sketch = newSketch(context, id + "F14", { "sketchPlane" : qUnion([Q0])});
            skLineSegment(sketch, "E92.bottom", {"start": v(40.41, 30) * mm, "end": v(54.56, 30) * mm});
            skLineSegment(sketch, "E92.top", {"start": v(40.41, 12) * mm, "end": v(54.56, 12) * mm});
            skLineSegment(sketch, "E92.left", {"start": v(40.41, 30) * mm, "end": v(40.41, 12) * mm});
            skLineSegment(sketch, "E92.right", {"start": v(54.56, 30) * mm, "end": v(54.56, 12) * mm});
            skLineSegment(sketch, "E93.0", {"start": v(42.34, 28.07) * mm, "end": v(46.52, 28.07) * mm});
            skLineSegment(sketch, "E93.1", {"start": v(42.34, 28.07) * mm, "end": v(42.34, 21.96) * mm});
            skLineSegment(sketch, "E93.2", {"start": v(42.34, 13.93) * mm, "end": v(46.52, 13.93) * mm});
            skLineSegment(sketch, "E93.3", {"start": v(52.63, 28.07) * mm, "end": v(52.63, 21.96) * mm});
            skLineSegment(sketch, "E94.left", {"start": v(46.52, 28.07) * mm, "end": v(46.52, 21.96) * mm});
            skLineSegment(sketch, "E94.right", {"start": v(48.45, 28.07) * mm, "end": v(48.45, 21.96) * mm});
            skLineSegment(sketch, "E95.bottom", {"start": v(52.63, 21.96) * mm, "end": v(48.45, 21.96) * mm});
            skLineSegment(sketch, "E95.top", {"start": v(52.63, 20.04) * mm, "end": v(48.45, 20.04) * mm});
            skLineSegment(sketch, "E96.trimOffspring", {"start": v(46.52, 21.96) * mm, "end": v(42.34, 21.96) * mm});
            skLineSegment(sketch, "E97.trimOffspring", {"start": v(46.52, 20.04) * mm, "end": v(46.52, 13.93) * mm});
            skLineSegment(sketch, "E98.trimOffspring", {"start": v(46.52, 20.04) * mm, "end": v(42.34, 20.04) * mm});
            skLineSegment(sketch, "E99.trimOffspring", {"start": v(48.45, 20.04) * mm, "end": v(48.45, 13.93) * mm});
            skLineSegment(sketch, "E100.trimOffspring", {"start": v(52.63, 20.04) * mm, "end": v(52.63, 13.93) * mm});
            skLineSegment(sketch, "E101.trimOffspring", {"start": v(42.34, 20.04) * mm, "end": v(42.34, 13.93) * mm});
            skLineSegment(sketch, "E102.trimOffspring", {"start": v(48.45, 28.07) * mm, "end": v(52.63, 28.07) * mm});
            skLineSegment(sketch, "E103.trimOffspring", {"start": v(48.45, 13.93) * mm, "end": v(52.63, 13.93) * mm});
            skLineSegment(sketch, "E104.bottom", {"start": v(54.56, 30) * mm, "end": v(68.7, 30) * mm});
            skLineSegment(sketch, "E104.top", {"start": v(54.56, 12) * mm, "end": v(68.7, 12) * mm});
            skLineSegment(sketch, "E104.right", {"start": v(68.7, 30) * mm, "end": v(68.7, 12) * mm});
            skLineSegment(sketch, "E105.0", {"start": v(56.49, 28.07) * mm, "end": v(60.66, 28.07) * mm});
            skLineSegment(sketch, "E105.1", {"start": v(56.49, 28.07) * mm, "end": v(56.49, 21.96) * mm});
            skLineSegment(sketch, "E105.2", {"start": v(56.49, 13.93) * mm, "end": v(60.66, 13.93) * mm});
            skLineSegment(sketch, "E105.3", {"start": v(66.77, 28.07) * mm, "end": v(66.77, 21.96) * mm});
            skLineSegment(sketch, "E106.left", {"start": v(60.66, 28.07) * mm, "end": v(60.66, 21.96) * mm});
            skLineSegment(sketch, "E106.right", {"start": v(62.6, 28.07) * mm, "end": v(62.6, 21.96) * mm});
            skLineSegment(sketch, "E107.bottom", {"start": v(66.77, 21.96) * mm, "end": v(62.6, 21.96) * mm});
            skLineSegment(sketch, "E107.top", {"start": v(66.77, 20.04) * mm, "end": v(62.6, 20.04) * mm});
            skLineSegment(sketch, "E108.trimOffspring", {"start": v(60.66, 21.96) * mm, "end": v(56.49, 21.96) * mm});
            skLineSegment(sketch, "E109.trimOffspring", {"start": v(60.66, 20.04) * mm, "end": v(60.66, 13.93) * mm});
            skLineSegment(sketch, "E110.trimOffspring", {"start": v(60.66, 20.04) * mm, "end": v(56.49, 20.04) * mm});
            skLineSegment(sketch, "E111.trimOffspring", {"start": v(62.6, 20.04) * mm, "end": v(62.6, 13.93) * mm});
            skLineSegment(sketch, "E112.trimOffspring", {"start": v(66.77, 20.04) * mm, "end": v(66.77, 13.93) * mm});
            skLineSegment(sketch, "E113.trimOffspring", {"start": v(56.49, 20.04) * mm, "end": v(56.49, 13.93) * mm});
            skLineSegment(sketch, "E114.trimOffspring", {"start": v(62.6, 28.07) * mm, "end": v(66.77, 28.07) * mm});
            skLineSegment(sketch, "E115.trimOffspring", {"start": v(62.6, 13.93) * mm, "end": v(66.77, 13.93) * mm});
            skSolve(sketch);
        }
        {
            var Q0;
            Q0=qSketchRegion(id+"F14",true);
            var Q1;
            Q1=qSketchRegion(id+"F13",true);
            var Q2;
            Q2=qSketchRegion(id+"F12",true);
            extrude(context, id + "F15", {"entities" : qUnion([Q0, Q1, Q2]), "operationType" : NewBodyOperationType.REMOVE, "oppositeDirection" : true, "depth" : .5 * mm, "offsetDistance" : 25 * mm});
        }
        {
            var Q0;
            {var subQ7=sQuery(id+"F0.wireOp",EDGE,"E0");Q0=makeQuery(id+"F7.boolean.opBoolean","SPLIT",FACE,{"disambiguationData":[TD([makeQuery(id+"F7.opExtrude","SWEPT_FACE",FACE,{"disambiguationData":[OSD([sQuery(id+"F4.wireOp",EDGE,"E20.6.0.0")])]})])],"derivedFrom":makeQuery(id+"F1.opExtrude","SWEPT_FACE",FACE,{"disambiguationData":[OSD([subQ7])]})});}
            var sketch = newSketch(context, id + "F16", { "sketchPlane" : qUnion([Q0])});
            skLineSegment(sketch, "E116.bottom", {"start": v(41.3, 30) * mm, "end": v(55.44, 30) * mm});
            skLineSegment(sketch, "E116.top", {"start": v(41.3, 12) * mm, "end": v(55.44, 12) * mm});
            skLineSegment(sketch, "E116.left", {"start": v(41.3, 30) * mm, "end": v(41.3, 12) * mm});
            skLineSegment(sketch, "E116.right", {"start": v(55.44, 30) * mm, "end": v(55.44, 12) * mm});
            skLineSegment(sketch, "E117.0", {"start": v(43.23, 28.07) * mm, "end": v(47.4, 28.07) * mm});
            skLineSegment(sketch, "E117.1", {"start": v(43.23, 28.07) * mm, "end": v(43.23, 21.96) * mm});
            skLineSegment(sketch, "E117.2", {"start": v(43.23, 13.93) * mm, "end": v(47.4, 13.93) * mm});
            skLineSegment(sketch, "E117.3", {"start": v(53.51, 28.07) * mm, "end": v(53.51, 21.96) * mm});
            skLineSegment(sketch, "E118.left", {"start": v(47.4, 28.07) * mm, "end": v(47.4, 21.96) * mm});
            skLineSegment(sketch, "E118.right", {"start": v(49.34, 28.07) * mm, "end": v(49.34, 21.96) * mm});
            skLineSegment(sketch, "E119.bottom", {"start": v(53.51, 21.96) * mm, "end": v(49.34, 21.96) * mm});
            skLineSegment(sketch, "E119.top", {"start": v(53.51, 20.04) * mm, "end": v(49.34, 20.04) * mm});
            skLineSegment(sketch, "E120.trimOffspring", {"start": v(47.4, 21.96) * mm, "end": v(43.23, 21.96) * mm});
            skLineSegment(sketch, "E121.trimOffspring", {"start": v(47.4, 20.04) * mm, "end": v(47.4, 13.93) * mm});
            skLineSegment(sketch, "E122.trimOffspring", {"start": v(47.4, 20.04) * mm, "end": v(43.23, 20.04) * mm});
            skLineSegment(sketch, "E123.trimOffspring", {"start": v(49.34, 20.04) * mm, "end": v(49.34, 13.93) * mm});
            skLineSegment(sketch, "E124.trimOffspring", {"start": v(53.51, 20.04) * mm, "end": v(53.51, 13.93) * mm});
            skLineSegment(sketch, "E125.trimOffspring", {"start": v(43.23, 20.04) * mm, "end": v(43.23, 13.93) * mm});
            skLineSegment(sketch, "E126.trimOffspring", {"start": v(49.34, 28.07) * mm, "end": v(53.51, 28.07) * mm});
            skLineSegment(sketch, "E127.trimOffspring", {"start": v(49.34, 13.93) * mm, "end": v(53.51, 13.93) * mm});
            skLineSegment(sketch, "E128.bottom", {"start": v(73.3, 30) * mm, "end": v(87.44, 30) * mm});
            skLineSegment(sketch, "E128.top", {"start": v(73.3, 12) * mm, "end": v(87.44, 12) * mm});
            skLineSegment(sketch, "E128.left", {"start": v(73.3, 30) * mm, "end": v(73.3, 12) * mm});
            skLineSegment(sketch, "E128.right", {"start": v(87.44, 30) * mm, "end": v(87.44, 12) * mm});
            skLineSegment(sketch, "E129.0", {"start": v(75.23, 28.07) * mm, "end": v(79.4, 28.07) * mm});
            skLineSegment(sketch, "E129.1", {"start": v(75.23, 28.07) * mm, "end": v(75.23, 21.96) * mm});
            skLineSegment(sketch, "E129.2", {"start": v(75.23, 13.93) * mm, "end": v(79.4, 13.93) * mm});
            skLineSegment(sketch, "E129.3", {"start": v(85.51, 28.07) * mm, "end": v(85.51, 21.96) * mm});
            skLineSegment(sketch, "E130.left", {"start": v(79.4, 28.07) * mm, "end": v(79.4, 21.96) * mm});
            skLineSegment(sketch, "E130.right", {"start": v(81.34, 28.07) * mm, "end": v(81.34, 21.96) * mm});
            skLineSegment(sketch, "E131.bottom", {"start": v(85.51, 21.96) * mm, "end": v(81.34, 21.96) * mm});
            skLineSegment(sketch, "E131.top", {"start": v(85.51, 20.04) * mm, "end": v(81.34, 20.04) * mm});
            skLineSegment(sketch, "E132.trimOffspring", {"start": v(79.4, 21.96) * mm, "end": v(75.23, 21.96) * mm});
            skLineSegment(sketch, "E133.trimOffspring", {"start": v(79.4, 20.04) * mm, "end": v(79.4, 13.93) * mm});
            skLineSegment(sketch, "E134.trimOffspring", {"start": v(79.4, 20.04) * mm, "end": v(75.23, 20.04) * mm});
            skLineSegment(sketch, "E135.trimOffspring", {"start": v(81.34, 20.04) * mm, "end": v(81.34, 13.93) * mm});
            skLineSegment(sketch, "E136.trimOffspring", {"start": v(85.51, 20.04) * mm, "end": v(85.51, 13.93) * mm});
            skLineSegment(sketch, "E137.trimOffspring", {"start": v(75.23, 20.04) * mm, "end": v(75.23, 13.93) * mm});
            skLineSegment(sketch, "E138.trimOffspring", {"start": v(81.34, 28.07) * mm, "end": v(85.51, 28.07) * mm});
            skLineSegment(sketch, "E139.trimOffspring", {"start": v(81.34, 13.93) * mm, "end": v(85.51, 13.93) * mm});
            skLineSegment(sketch, "E140.bottom", {"start": v(105.3, 30) * mm, "end": v(119.44, 30) * mm});
            skLineSegment(sketch, "E140.top", {"start": v(105.3, 12) * mm, "end": v(119.44, 12) * mm});
            skLineSegment(sketch, "E140.left", {"start": v(105.3, 30) * mm, "end": v(105.3, 12) * mm});
            skLineSegment(sketch, "E140.right", {"start": v(119.44, 30) * mm, "end": v(119.44, 12) * mm});
            skLineSegment(sketch, "E141.0", {"start": v(107.23, 28.07) * mm, "end": v(111.4, 28.07) * mm});
            skLineSegment(sketch, "E141.1", {"start": v(107.23, 28.07) * mm, "end": v(107.23, 21.96) * mm});
            skLineSegment(sketch, "E141.2", {"start": v(107.23, 13.93) * mm, "end": v(111.4, 13.93) * mm});
            skLineSegment(sketch, "E141.3", {"start": v(117.51, 28.07) * mm, "end": v(117.51, 21.96) * mm});
            skLineSegment(sketch, "E142.left", {"start": v(111.4, 28.07) * mm, "end": v(111.4, 21.96) * mm});
            skLineSegment(sketch, "E142.right", {"start": v(113.34, 28.07) * mm, "end": v(113.34, 21.96) * mm});
            skLineSegment(sketch, "E143.bottom", {"start": v(117.51, 21.96) * mm, "end": v(113.34, 21.96) * mm});
            skLineSegment(sketch, "E143.top", {"start": v(117.51, 20.04) * mm, "end": v(113.34, 20.04) * mm});
            skLineSegment(sketch, "E144.trimOffspring", {"start": v(111.4, 21.96) * mm, "end": v(107.23, 21.96) * mm});
            skLineSegment(sketch, "E145.trimOffspring", {"start": v(111.4, 20.04) * mm, "end": v(111.4, 13.93) * mm});
            skLineSegment(sketch, "E146.trimOffspring", {"start": v(111.4, 20.04) * mm, "end": v(107.23, 20.04) * mm});
            skLineSegment(sketch, "E147.trimOffspring", {"start": v(113.34, 20.04) * mm, "end": v(113.34, 13.93) * mm});
            skLineSegment(sketch, "E148.trimOffspring", {"start": v(117.51, 20.04) * mm, "end": v(117.51, 13.93) * mm});
            skLineSegment(sketch, "E149.trimOffspring", {"start": v(107.23, 20.04) * mm, "end": v(107.23, 13.93) * mm});
            skLineSegment(sketch, "E150.trimOffspring", {"start": v(113.34, 28.07) * mm, "end": v(117.51, 28.07) * mm});
            skLineSegment(sketch, "E151.trimOffspring", {"start": v(113.34, 13.93) * mm, "end": v(117.51, 13.93) * mm});
            skLineSegment(sketch, "E152.bottom", {"start": v(137.3, 30) * mm, "end": v(151.44, 30) * mm});
            skLineSegment(sketch, "E152.top", {"start": v(137.3, 12) * mm, "end": v(151.44, 12) * mm});
            skLineSegment(sketch, "E152.left", {"start": v(137.3, 30) * mm, "end": v(137.3, 12) * mm});
            skLineSegment(sketch, "E152.right", {"start": v(151.44, 30) * mm, "end": v(151.44, 12) * mm});
            skLineSegment(sketch, "E153.0", {"start": v(139.23, 28.07) * mm, "end": v(143.4, 28.07) * mm});
            skLineSegment(sketch, "E153.1", {"start": v(139.23, 28.07) * mm, "end": v(139.23, 21.96) * mm});
            skLineSegment(sketch, "E153.2", {"start": v(139.23, 13.93) * mm, "end": v(143.4, 13.93) * mm});
            skLineSegment(sketch, "E153.3", {"start": v(149.51, 28.07) * mm, "end": v(149.51, 21.96) * mm});
            skLineSegment(sketch, "E154.left", {"start": v(143.4, 28.07) * mm, "end": v(143.4, 21.96) * mm});
            skLineSegment(sketch, "E154.right", {"start": v(145.34, 28.07) * mm, "end": v(145.34, 21.96) * mm});
            skLineSegment(sketch, "E155.bottom", {"start": v(149.51, 21.96) * mm, "end": v(145.34, 21.96) * mm});
            skLineSegment(sketch, "E155.top", {"start": v(149.51, 20.04) * mm, "end": v(145.34, 20.04) * mm});
            skLineSegment(sketch, "E156.trimOffspring", {"start": v(143.4, 21.96) * mm, "end": v(139.23, 21.96) * mm});
            skLineSegment(sketch, "E157.trimOffspring", {"start": v(143.4, 20.04) * mm, "end": v(143.4, 13.93) * mm});
            skLineSegment(sketch, "E158.trimOffspring", {"start": v(143.4, 20.04) * mm, "end": v(139.23, 20.04) * mm});
            skLineSegment(sketch, "E159.trimOffspring", {"start": v(145.34, 20.04) * mm, "end": v(145.34, 13.93) * mm});
            skLineSegment(sketch, "E160.trimOffspring", {"start": v(149.51, 20.04) * mm, "end": v(149.51, 13.93) * mm});
            skLineSegment(sketch, "E161.trimOffspring", {"start": v(139.23, 20.04) * mm, "end": v(139.23, 13.93) * mm});
            skLineSegment(sketch, "E162.trimOffspring", {"start": v(145.34, 28.07) * mm, "end": v(149.51, 28.07) * mm});
            skLineSegment(sketch, "E163.trimOffspring", {"start": v(145.34, 13.93) * mm, "end": v(149.51, 13.93) * mm});
            skLineSegment(sketch, "E164.bottom", {"start": v(169.3, 30) * mm, "end": v(183.44, 30) * mm});
            skLineSegment(sketch, "E164.top", {"start": v(169.3, 12) * mm, "end": v(183.44, 12) * mm});
            skLineSegment(sketch, "E164.left", {"start": v(169.3, 30) * mm, "end": v(169.3, 12) * mm});
            skLineSegment(sketch, "E164.right", {"start": v(183.44, 30) * mm, "end": v(183.44, 12) * mm});
            skLineSegment(sketch, "E165.0", {"start": v(171.23, 28.07) * mm, "end": v(175.4, 28.07) * mm});
            skLineSegment(sketch, "E165.1", {"start": v(171.23, 28.07) * mm, "end": v(171.23, 21.96) * mm});
            skLineSegment(sketch, "E165.2", {"start": v(171.23, 13.93) * mm, "end": v(175.4, 13.93) * mm});
            skLineSegment(sketch, "E165.3", {"start": v(181.51, 28.07) * mm, "end": v(181.51, 21.96) * mm});
            skLineSegment(sketch, "E166.left", {"start": v(175.4, 28.07) * mm, "end": v(175.4, 21.96) * mm});
            skLineSegment(sketch, "E166.right", {"start": v(177.34, 28.07) * mm, "end": v(177.34, 21.96) * mm});
            skLineSegment(sketch, "E167.bottom", {"start": v(181.51, 21.96) * mm, "end": v(177.34, 21.96) * mm});
            skLineSegment(sketch, "E167.top", {"start": v(181.51, 20.04) * mm, "end": v(177.34, 20.04) * mm});
            skLineSegment(sketch, "E168.trimOffspring", {"start": v(175.4, 21.96) * mm, "end": v(171.23, 21.96) * mm});
            skLineSegment(sketch, "E169.trimOffspring", {"start": v(175.4, 20.04) * mm, "end": v(175.4, 13.93) * mm});
            skLineSegment(sketch, "E170.trimOffspring", {"start": v(175.4, 20.04) * mm, "end": v(171.23, 20.04) * mm});
            skLineSegment(sketch, "E171.trimOffspring", {"start": v(177.34, 20.04) * mm, "end": v(177.34, 13.93) * mm});
            skLineSegment(sketch, "E172.trimOffspring", {"start": v(181.51, 20.04) * mm, "end": v(181.51, 13.93) * mm});
            skLineSegment(sketch, "E173.trimOffspring", {"start": v(171.23, 20.04) * mm, "end": v(171.23, 13.93) * mm});
            skLineSegment(sketch, "E174.trimOffspring", {"start": v(177.34, 28.07) * mm, "end": v(181.51, 28.07) * mm});
            skLineSegment(sketch, "E175.trimOffspring", {"start": v(177.34, 13.93) * mm, "end": v(181.51, 13.93) * mm});
            skLineSegment(sketch, "E176.bottom", {"start": v(201.3, 30) * mm, "end": v(215.44, 30) * mm});
            skLineSegment(sketch, "E176.top", {"start": v(201.3, 12) * mm, "end": v(215.44, 12) * mm});
            skLineSegment(sketch, "E176.left", {"start": v(201.3, 30) * mm, "end": v(201.3, 12) * mm});
            skLineSegment(sketch, "E176.right", {"start": v(215.44, 30) * mm, "end": v(215.44, 12) * mm});
            skLineSegment(sketch, "E177.0", {"start": v(203.23, 28.07) * mm, "end": v(207.4, 28.07) * mm});
            skLineSegment(sketch, "E177.1", {"start": v(203.23, 28.07) * mm, "end": v(203.23, 21.96) * mm});
            skLineSegment(sketch, "E177.2", {"start": v(203.23, 13.93) * mm, "end": v(207.4, 13.93) * mm});
            skLineSegment(sketch, "E177.3", {"start": v(213.51, 28.07) * mm, "end": v(213.51, 21.96) * mm});
            skLineSegment(sketch, "E178.left", {"start": v(207.4, 28.07) * mm, "end": v(207.4, 21.96) * mm});
            skLineSegment(sketch, "E178.right", {"start": v(209.34, 28.07) * mm, "end": v(209.34, 21.96) * mm});
            skLineSegment(sketch, "E179.bottom", {"start": v(213.51, 21.96) * mm, "end": v(209.34, 21.96) * mm});
            skLineSegment(sketch, "E179.top", {"start": v(213.51, 20.04) * mm, "end": v(209.34, 20.04) * mm});
            skLineSegment(sketch, "E180.trimOffspring", {"start": v(207.4, 21.96) * mm, "end": v(203.23, 21.96) * mm});
            skLineSegment(sketch, "E181.trimOffspring", {"start": v(207.4, 20.04) * mm, "end": v(207.4, 13.93) * mm});
            skLineSegment(sketch, "E182.trimOffspring", {"start": v(207.4, 20.04) * mm, "end": v(203.23, 20.04) * mm});
            skLineSegment(sketch, "E183.trimOffspring", {"start": v(209.34, 20.04) * mm, "end": v(209.34, 13.93) * mm});
            skLineSegment(sketch, "E184.trimOffspring", {"start": v(213.51, 20.04) * mm, "end": v(213.51, 13.93) * mm});
            skLineSegment(sketch, "E185.trimOffspring", {"start": v(203.23, 20.04) * mm, "end": v(203.23, 13.93) * mm});
            skLineSegment(sketch, "E186.trimOffspring", {"start": v(209.34, 28.07) * mm, "end": v(213.51, 28.07) * mm});
            skLineSegment(sketch, "E187.trimOffspring", {"start": v(209.34, 13.93) * mm, "end": v(213.51, 13.93) * mm});
            skLineSegment(sketch, "E188.left", {"start": v(215.44, 31.5) * mm, "end": v(215.44, 13.5) * mm});
            skSolve(sketch);
        }
        {
            var Q0;
            Q0=qSketchRegion(id+"F16",true);
            extrude(context, id + "F17", {"entities" : qUnion([Q0]), "operationType" : NewBodyOperationType.REMOVE, "oppositeDirection" : true, "depth" : .5 * mm, "offsetDistance" : 25 * mm});
        }
        {
            var Q0;
            {var subQ5=sQuery(id+"F0.wireOp",EDGE,"E2");Q0=makeQuery(id+"F9.boolean.opBoolean","SPLIT",FACE,{"disambiguationData":[TD([makeQuery(id+"F9.opExtrude","SWEPT_FACE",FACE,{"disambiguationData":[OSD([sQuery(id+"F6.wireOp",EDGE,"E38.1.0.0")])]})])],"derivedFrom":makeQuery(id+"F1.opExtrude","SWEPT_FACE",FACE,{"disambiguationData":[OSD([subQ5])]})});}
            var sketch = newSketch(context, id + "F18", { "sketchPlane" : qUnion([Q0])});
            skLineSegment(sketch, "E189.bottom", {"start": v(-215.7, 30) * mm, "end": v(-201.56, 30) * mm});
            skLineSegment(sketch, "E189.top", {"start": v(-215.7, 12) * mm, "end": v(-201.56, 12) * mm});
            skLineSegment(sketch, "E189.left", {"start": v(-215.7, 30) * mm, "end": v(-215.7, 12) * mm});
            skLineSegment(sketch, "E189.right", {"start": v(-201.56, 30) * mm, "end": v(-201.56, 12) * mm});
            skLineSegment(sketch, "E190.0", {"start": v(-213.77, 28.07) * mm, "end": v(-209.6, 28.07) * mm});
            skLineSegment(sketch, "E190.1", {"start": v(-213.77, 28.07) * mm, "end": v(-213.77, 21.96) * mm});
            skLineSegment(sketch, "E190.2", {"start": v(-213.77, 13.93) * mm, "end": v(-209.6, 13.93) * mm});
            skLineSegment(sketch, "E190.3", {"start": v(-203.49, 28.07) * mm, "end": v(-203.49, 21.96) * mm});
            skLineSegment(sketch, "E191.left", {"start": v(-209.6, 28.07) * mm, "end": v(-209.6, 21.96) * mm});
            skLineSegment(sketch, "E191.right", {"start": v(-207.66, 28.07) * mm, "end": v(-207.66, 21.96) * mm});
            skLineSegment(sketch, "E192.bottom", {"start": v(-203.49, 21.96) * mm, "end": v(-207.66, 21.96) * mm});
            skLineSegment(sketch, "E192.top", {"start": v(-203.49, 20.04) * mm, "end": v(-207.66, 20.04) * mm});
            skLineSegment(sketch, "E193.trimOffspring", {"start": v(-209.6, 21.96) * mm, "end": v(-213.77, 21.96) * mm});
            skLineSegment(sketch, "E194.trimOffspring", {"start": v(-209.6, 20.04) * mm, "end": v(-209.6, 13.93) * mm});
            skLineSegment(sketch, "E195.trimOffspring", {"start": v(-209.6, 20.04) * mm, "end": v(-213.77, 20.04) * mm});
            skLineSegment(sketch, "E196.trimOffspring", {"start": v(-207.66, 20.04) * mm, "end": v(-207.66, 13.93) * mm});
            skLineSegment(sketch, "E197.trimOffspring", {"start": v(-203.49, 20.04) * mm, "end": v(-203.49, 13.93) * mm});
            skLineSegment(sketch, "E198.trimOffspring", {"start": v(-213.77, 20.04) * mm, "end": v(-213.77, 13.93) * mm});
            skLineSegment(sketch, "E199.trimOffspring", {"start": v(-207.66, 28.07) * mm, "end": v(-203.49, 28.07) * mm});
            skLineSegment(sketch, "E200.trimOffspring", {"start": v(-207.66, 13.93) * mm, "end": v(-203.49, 13.93) * mm});
            skLineSegment(sketch, "E201.bottom", {"start": v(-183.7, 30) * mm, "end": v(-169.56, 30) * mm});
            skLineSegment(sketch, "E201.top", {"start": v(-183.7, 12) * mm, "end": v(-169.56, 12) * mm});
            skLineSegment(sketch, "E201.left", {"start": v(-183.7, 30) * mm, "end": v(-183.7, 12) * mm});
            skLineSegment(sketch, "E201.right", {"start": v(-169.56, 30) * mm, "end": v(-169.56, 12) * mm});
            skLineSegment(sketch, "E202.0", {"start": v(-181.77, 28.07) * mm, "end": v(-177.6, 28.07) * mm});
            skLineSegment(sketch, "E202.1", {"start": v(-181.77, 28.07) * mm, "end": v(-181.77, 21.96) * mm});
            skLineSegment(sketch, "E202.2", {"start": v(-181.77, 13.93) * mm, "end": v(-177.6, 13.93) * mm});
            skLineSegment(sketch, "E202.3", {"start": v(-171.49, 28.07) * mm, "end": v(-171.49, 21.96) * mm});
            skLineSegment(sketch, "E203.left", {"start": v(-177.6, 28.07) * mm, "end": v(-177.6, 21.96) * mm});
            skLineSegment(sketch, "E203.right", {"start": v(-175.66, 28.07) * mm, "end": v(-175.66, 21.96) * mm});
            skLineSegment(sketch, "E204.bottom", {"start": v(-171.49, 21.96) * mm, "end": v(-175.66, 21.96) * mm});
            skLineSegment(sketch, "E204.top", {"start": v(-171.49, 20.04) * mm, "end": v(-175.66, 20.04) * mm});
            skLineSegment(sketch, "E205.trimOffspring", {"start": v(-177.6, 21.96) * mm, "end": v(-181.77, 21.96) * mm});
            skLineSegment(sketch, "E206.trimOffspring", {"start": v(-177.6, 20.04) * mm, "end": v(-177.6, 13.93) * mm});
            skLineSegment(sketch, "E207.trimOffspring", {"start": v(-177.6, 20.04) * mm, "end": v(-181.77, 20.04) * mm});
            skLineSegment(sketch, "E208.trimOffspring", {"start": v(-175.66, 20.04) * mm, "end": v(-175.66, 13.93) * mm});
            skLineSegment(sketch, "E209.trimOffspring", {"start": v(-171.49, 20.04) * mm, "end": v(-171.49, 13.93) * mm});
            skLineSegment(sketch, "E210.trimOffspring", {"start": v(-181.77, 20.04) * mm, "end": v(-181.77, 13.93) * mm});
            skLineSegment(sketch, "E211.trimOffspring", {"start": v(-175.66, 28.07) * mm, "end": v(-171.49, 28.07) * mm});
            skLineSegment(sketch, "E212.trimOffspring", {"start": v(-175.66, 13.93) * mm, "end": v(-171.49, 13.93) * mm});
            skLineSegment(sketch, "E213.bottom", {"start": v(-151.7, 30) * mm, "end": v(-137.56, 30) * mm});
            skLineSegment(sketch, "E213.top", {"start": v(-151.7, 12) * mm, "end": v(-137.56, 12) * mm});
            skLineSegment(sketch, "E213.left", {"start": v(-151.7, 30) * mm, "end": v(-151.7, 12) * mm});
            skLineSegment(sketch, "E213.right", {"start": v(-137.56, 30) * mm, "end": v(-137.56, 12) * mm});
            skLineSegment(sketch, "E214.0", {"start": v(-149.77, 28.07) * mm, "end": v(-145.6, 28.07) * mm});
            skLineSegment(sketch, "E214.1", {"start": v(-149.77, 28.07) * mm, "end": v(-149.77, 21.96) * mm});
            skLineSegment(sketch, "E214.2", {"start": v(-149.77, 13.93) * mm, "end": v(-145.6, 13.93) * mm});
            skLineSegment(sketch, "E214.3", {"start": v(-139.49, 28.07) * mm, "end": v(-139.49, 21.96) * mm});
            skLineSegment(sketch, "E215.left", {"start": v(-145.6, 28.07) * mm, "end": v(-145.6, 21.96) * mm});
            skLineSegment(sketch, "E215.right", {"start": v(-143.66, 28.07) * mm, "end": v(-143.66, 21.96) * mm});
            skLineSegment(sketch, "E216.bottom", {"start": v(-139.49, 21.96) * mm, "end": v(-143.66, 21.96) * mm});
            skLineSegment(sketch, "E216.top", {"start": v(-139.49, 20.04) * mm, "end": v(-143.66, 20.04) * mm});
            skLineSegment(sketch, "E217.trimOffspring", {"start": v(-145.6, 21.96) * mm, "end": v(-149.77, 21.96) * mm});
            skLineSegment(sketch, "E218.trimOffspring", {"start": v(-145.6, 20.04) * mm, "end": v(-145.6, 13.93) * mm});
            skLineSegment(sketch, "E219.trimOffspring", {"start": v(-145.6, 20.04) * mm, "end": v(-149.77, 20.04) * mm});
            skLineSegment(sketch, "E220.trimOffspring", {"start": v(-143.66, 20.04) * mm, "end": v(-143.66, 13.93) * mm});
            skLineSegment(sketch, "E221.trimOffspring", {"start": v(-139.49, 20.04) * mm, "end": v(-139.49, 13.93) * mm});
            skLineSegment(sketch, "E222.trimOffspring", {"start": v(-149.77, 20.04) * mm, "end": v(-149.77, 13.93) * mm});
            skLineSegment(sketch, "E223.trimOffspring", {"start": v(-143.66, 28.07) * mm, "end": v(-139.49, 28.07) * mm});
            skLineSegment(sketch, "E224.trimOffspring", {"start": v(-143.66, 13.93) * mm, "end": v(-139.49, 13.93) * mm});
            skLineSegment(sketch, "E225.left", {"start": v(-137.56, 30.15) * mm, "end": v(-137.56, 12.15) * mm});
            skLineSegment(sketch, "E226.bottom", {"start": v(-119.7, 30) * mm, "end": v(-105.56, 30) * mm});
            skLineSegment(sketch, "E226.top", {"start": v(-119.7, 12) * mm, "end": v(-105.56, 12) * mm});
            skLineSegment(sketch, "E226.left", {"start": v(-119.7, 30) * mm, "end": v(-119.7, 12) * mm});
            skLineSegment(sketch, "E226.right", {"start": v(-105.56, 30) * mm, "end": v(-105.56, 12) * mm});
            skLineSegment(sketch, "E227.0", {"start": v(-117.77, 28.07) * mm, "end": v(-113.6, 28.07) * mm});
            skLineSegment(sketch, "E227.1", {"start": v(-117.77, 28.07) * mm, "end": v(-117.77, 21.96) * mm});
            skLineSegment(sketch, "E227.2", {"start": v(-117.77, 13.93) * mm, "end": v(-113.6, 13.93) * mm});
            skLineSegment(sketch, "E227.3", {"start": v(-107.49, 28.07) * mm, "end": v(-107.49, 21.96) * mm});
            skLineSegment(sketch, "E228.left", {"start": v(-113.6, 28.07) * mm, "end": v(-113.6, 21.96) * mm});
            skLineSegment(sketch, "E228.right", {"start": v(-111.66, 28.07) * mm, "end": v(-111.66, 21.96) * mm});
            skLineSegment(sketch, "E229.bottom", {"start": v(-107.49, 21.96) * mm, "end": v(-111.66, 21.96) * mm});
            skLineSegment(sketch, "E229.top", {"start": v(-107.49, 20.04) * mm, "end": v(-111.66, 20.04) * mm});
            skLineSegment(sketch, "E230.trimOffspring", {"start": v(-113.6, 21.96) * mm, "end": v(-117.77, 21.96) * mm});
            skLineSegment(sketch, "E231.trimOffspring", {"start": v(-113.6, 20.04) * mm, "end": v(-113.6, 13.93) * mm});
            skLineSegment(sketch, "E232.trimOffspring", {"start": v(-113.6, 20.04) * mm, "end": v(-117.77, 20.04) * mm});
            skLineSegment(sketch, "E233.trimOffspring", {"start": v(-111.66, 20.04) * mm, "end": v(-111.66, 13.93) * mm});
            skLineSegment(sketch, "E234.trimOffspring", {"start": v(-107.49, 20.04) * mm, "end": v(-107.49, 13.93) * mm});
            skLineSegment(sketch, "E235.trimOffspring", {"start": v(-117.77, 20.04) * mm, "end": v(-117.77, 13.93) * mm});
            skLineSegment(sketch, "E236.trimOffspring", {"start": v(-111.66, 28.07) * mm, "end": v(-107.49, 28.07) * mm});
            skLineSegment(sketch, "E237.trimOffspring", {"start": v(-111.66, 13.93) * mm, "end": v(-107.49, 13.93) * mm});
            skLineSegment(sketch, "E238.left", {"start": v(-105.56, 31.3) * mm, "end": v(-105.56, 13.3) * mm});
            skLineSegment(sketch, "E239.bottom", {"start": v(-87.7, 30) * mm, "end": v(-73.56, 30) * mm});
            skLineSegment(sketch, "E239.top", {"start": v(-87.7, 12) * mm, "end": v(-73.56, 12) * mm});
            skLineSegment(sketch, "E239.left", {"start": v(-87.7, 30) * mm, "end": v(-87.7, 12) * mm});
            skLineSegment(sketch, "E239.right", {"start": v(-73.56, 30) * mm, "end": v(-73.56, 12) * mm});
            skLineSegment(sketch, "E240.0", {"start": v(-85.77, 28.07) * mm, "end": v(-81.6, 28.07) * mm});
            skLineSegment(sketch, "E240.1", {"start": v(-85.77, 28.07) * mm, "end": v(-85.77, 21.96) * mm});
            skLineSegment(sketch, "E240.2", {"start": v(-85.77, 13.93) * mm, "end": v(-81.6, 13.93) * mm});
            skLineSegment(sketch, "E240.3", {"start": v(-75.49, 28.07) * mm, "end": v(-75.49, 21.96) * mm});
            skLineSegment(sketch, "E241.left", {"start": v(-81.6, 28.07) * mm, "end": v(-81.6, 21.96) * mm});
            skLineSegment(sketch, "E241.right", {"start": v(-79.66, 28.07) * mm, "end": v(-79.66, 21.96) * mm});
            skLineSegment(sketch, "E242.bottom", {"start": v(-75.49, 21.96) * mm, "end": v(-79.66, 21.96) * mm});
            skLineSegment(sketch, "E242.top", {"start": v(-75.49, 20.04) * mm, "end": v(-79.66, 20.04) * mm});
            skLineSegment(sketch, "E243.trimOffspring", {"start": v(-81.6, 21.96) * mm, "end": v(-85.77, 21.96) * mm});
            skLineSegment(sketch, "E244.trimOffspring", {"start": v(-81.6, 20.04) * mm, "end": v(-81.6, 13.93) * mm});
            skLineSegment(sketch, "E245.trimOffspring", {"start": v(-81.6, 20.04) * mm, "end": v(-85.77, 20.04) * mm});
            skLineSegment(sketch, "E246.trimOffspring", {"start": v(-79.66, 20.04) * mm, "end": v(-79.66, 13.93) * mm});
            skLineSegment(sketch, "E247.trimOffspring", {"start": v(-75.49, 20.04) * mm, "end": v(-75.49, 13.93) * mm});
            skLineSegment(sketch, "E248.trimOffspring", {"start": v(-85.77, 20.04) * mm, "end": v(-85.77, 13.93) * mm});
            skLineSegment(sketch, "E249.trimOffspring", {"start": v(-79.66, 28.07) * mm, "end": v(-75.49, 28.07) * mm});
            skLineSegment(sketch, "E250.trimOffspring", {"start": v(-79.66, 13.93) * mm, "end": v(-75.49, 13.93) * mm});
            skLineSegment(sketch, "E251.left", {"start": v(-73.56, 31.52) * mm, "end": v(-73.56, 13.52) * mm});
            skSolve(sketch);
        }
        {
            var Q0;
            Q0=qSketchRegion(id+"F18",true);
            extrude(context, id + "F19", {"entities" : qUnion([Q0]), "operationType" : NewBodyOperationType.REMOVE, "oppositeDirection" : true, "depth" : .5 * mm, "offsetDistance" : 25 * mm});
        }
    });
